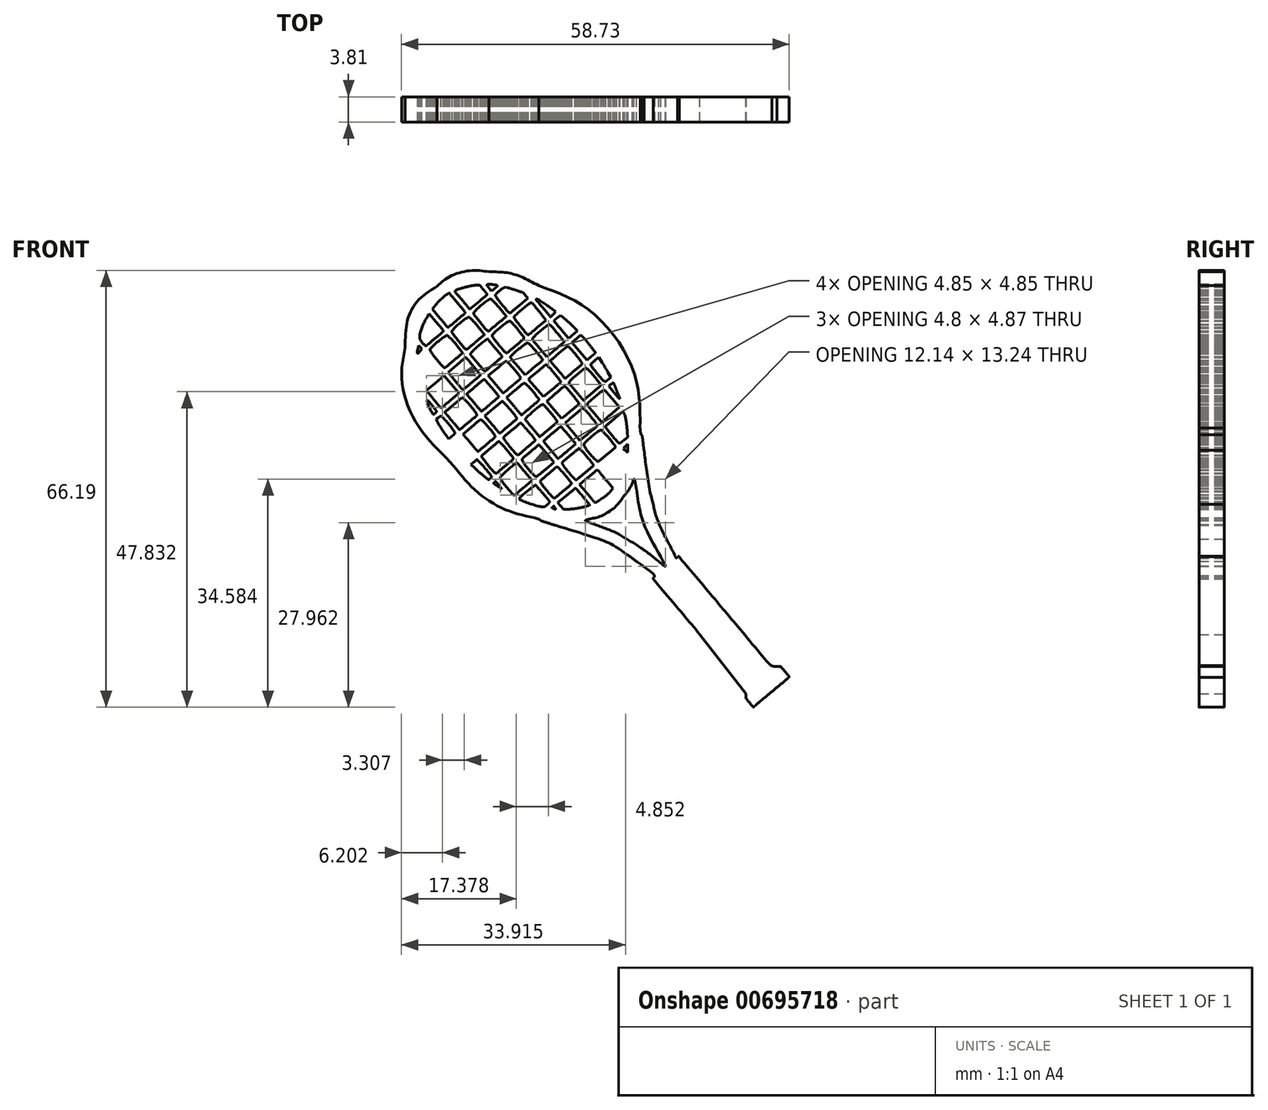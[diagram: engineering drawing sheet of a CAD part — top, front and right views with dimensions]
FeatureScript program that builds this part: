
annotation { "Feature Type Name" : "Feature", "Feature Type Description" : "" }
export const myFeature = defineFeature(function(context is Context, id is Id, definition is map)
    precondition{}
    {
        {
            var Q0;
            Q0=qCreatedBy(makeId("Front.planeOp"),FACE);
            var sketch = newSketch(context, id + "F0", { "sketchPlane" : qUnion([Q0])});
            skFitSpline(sketch, "E0", {"points": [v(8.3, -34.6) * mm, v(7.75, -33.92) * mm, v(7.73, -33.88) * mm, v(7.73, -33.21) * mm]});
            skFitSpline(sketch, "E1", {"points": [v(0.8, -24.26) * mm, v(-3.02, -19.72) * mm, v(-6.18, -15.94) * mm, v(-6.23, -15.86) * mm]});
            skFitSpline(sketch, "E2", {"points": [v(-6.23, -15.86) * mm, v(-6.27, -15.78) * mm, v(-6.25, -15.65) * mm, v(-6.18, -15.57) * mm]});
            skFitSpline(sketch, "E3", {"points": [v(-6.18, -15.57) * mm, v(-6.11, -15.48) * mm, v(-6.09, -15.36) * mm, v(-6.12, -15.3) * mm]});
            skFitSpline(sketch, "E4", {"points": [v(-6.12, -15.3) * mm, v(-6.22, -15.14) * mm, v(-8.37, -13.48) * mm, v(-9.44, -12.74) * mm]});
            skFitSpline(sketch, "E5", {"points": [v(-9.44, -12.74) * mm, v(-12.31, -10.75) * mm, v(-14.7, -9.72) * mm, v(-21.08, -7.72) * mm]});
            skFitSpline(sketch, "E6", {"points": [v(-21.08, -7.72) * mm, v(-22.32, -7.33) * mm, v(-23.37, -6.97) * mm, v(-23.4, -6.91) * mm]});
            skFitSpline(sketch, "E7", {"points": [v(-23.4, -6.91) * mm, v(-23.44, -6.86) * mm, v(-23.84, -6.7) * mm, v(-24.3, -6.57) * mm]});
            skFitSpline(sketch, "E8", {"points": [v(-24.3, -6.57) * mm, v(-28.9, -5.24) * mm, v(-33.33, -2.3) * mm, v(-37.04, 1.88) * mm]});
            skFitSpline(sketch, "E9", {"points": [v(-37.04, 1.88) * mm, v(-41.78, 7.22) * mm, v(-44.33, 13.72) * mm, v(-43.87, 19.25) * mm]});
            skFitSpline(sketch, "E10", {"points": [v(-43.87, 19.25) * mm, v(-43.53, 23.3) * mm, v(-41.98, 26.27) * mm, v(-39.04, 28.52) * mm]});
            skFitSpline(sketch, "E11", {"points": [v(-39.04, 28.52) * mm, v(-37.1, 30) * mm, v(-33.96, 30.88) * mm, v(-31.18, 30.72) * mm]});
            skFitSpline(sketch, "E12", {"points": [v(-31.18, 30.72) * mm, v(-28.5, 30.57) * mm, v(-26.4, 29.98) * mm, v(-23.61, 28.6) * mm]});
            skFitSpline(sketch, "E13", {"points": [v(-23.61, 28.6) * mm, v(-15.7, 24.66) * mm, v(-9.26, 15.6) * mm, v(-8.28, 7.03) * mm]});
            skFitSpline(sketch, "E14", {"points": [v(-8.28, 7.03) * mm, v(-8.22, 6.51) * mm, v(-8.13, 6.07) * mm, v(-8.08, 6.03) * mm]});
            skFitSpline(sketch, "E15", {"points": [v(-8.08, 6.03) * mm, v(-8.02, 6) * mm, v(-7.85, 4.93) * mm, v(-7.68, 3.65) * mm]});
            skFitSpline(sketch, "E16", {"points": [v(-7.68, 3.65) * mm, v(-7.3, 0.68) * mm, v(-6.69, -2.97) * mm, v(-6.3, -4.53) * mm]});
            skFitSpline(sketch, "E17", {"points": [v(-6.3, -4.53) * mm, v(-5.88, -6.16) * mm, v(-5.03, -8.3) * mm, v(-3.9, -10.52) * mm]});
            skFitSpline(sketch, "E18", {"points": [v(-3.9, -10.52) * mm, v(-2.82, -12.66) * mm, v(-2.8, -12.7) * mm, v(-2.57, -12.5) * mm]});
            skFitSpline(sketch, "E19", {"points": [v(-2.57, -12.5) * mm, v(-2.47, -12.42) * mm, v(-2.39, -12.42) * mm, v(-2.34, -12.49) * mm]});
            skFitSpline(sketch, "E20", {"points": [v(-2.34, -12.49) * mm, v(-2.3, -12.55) * mm, v(0.81, -16.27) * mm, v(4.58, -20.75) * mm]});
            skFitSpline(sketch, "E21", {"points": [v(4.58, -20.75) * mm, v(8.42, -25.33) * mm, v(11.53, -28.94) * mm, v(11.68, -29) * mm]});
            skFitSpline(sketch, "E22", {"points": [v(11.68, -29) * mm, v(11.82, -29.05) * mm, v(12.19, -29.1) * mm, v(12.48, -29.1) * mm]});
            skFitSpline(sketch, "E23", {"points": [v(12.48, -29.1) * mm, v(13.02, -29.1) * mm, v(13.03, -29.1) * mm, v(13.7, -29.89) * mm]});
            skFitSpline(sketch, "E24", {"points": [v(13.7, -29.89) * mm, v(14.06, -30.33) * mm, v(14.32, -30.72) * mm, v(14.28, -30.76) * mm]});
            skFitSpline(sketch, "E25", {"points": [v(14.28, -30.76) * mm, v(14.23, -30.8) * mm, v(13.1, -31.74) * mm, v(11.76, -32.85) * mm]});
            skFitSpline(sketch, "E26", {"points": [v(11.76, -32.85) * mm, v(10.43, -33.96) * mm, v(9.23, -34.97) * mm, v(9.1, -35.08) * mm]});
            skFitSpline(sketch, "E27", {"points": [v(9.1, -35.08) * mm, v(8.87, -35.29) * mm, v(8.86, -35.28) * mm, v(8.3, -34.6) * mm]});
            skLineSegment(sketch, "E28", {"start": v(7.73, -33.21) * mm, "end": v(7.73, -32.53) * mm});
            skLineSegment(sketch, "E29", {"start": v(0.8, -24.26) * mm, "end": v(7.73, -33.21) * mm});
            skFitSpline(sketch, "E30", {"points": [v(-5.17, -12.46) * mm, v(-7.27, -8.56) * mm, v(-8.18, -6.01) * mm, v(-8.85, -2.18) * mm]});
            skFitSpline(sketch, "E31", {"points": [v(-8.85, -2.18) * mm, v(-9, -1.37) * mm, v(-9.14, -0.71) * mm, v(-9.18, -0.71) * mm]});
            skFitSpline(sketch, "E32", {"points": [v(-9.18, -0.71) * mm, v(-9.22, -0.71) * mm, v(-9.3, -0.87) * mm, v(-9.38, -1.07) * mm]});
            skFitSpline(sketch, "E33", {"points": [v(-9.38, -1.07) * mm, v(-9.55, -1.57) * mm, v(-10.2, -2.63) * mm, v(-10.85, -3.45) * mm]});
            skFitSpline(sketch, "E34", {"points": [v(-10.85, -3.45) * mm, v(-11.95, -4.84) * mm, v(-14.11, -6.26) * mm, v(-15.87, -6.74) * mm]});
            skFitSpline(sketch, "E35", {"points": [v(-15.87, -6.74) * mm, v(-16.25, -6.85) * mm, v(-16.56, -6.96) * mm, v(-16.56, -7) * mm]});
            skFitSpline(sketch, "E36", {"points": [v(-16.56, -7) * mm, v(-16.56, -7.04) * mm, v(-15.9, -7.31) * mm, v(-15.1, -7.6) * mm]});
            skFitSpline(sketch, "E37", {"points": [v(-15.1, -7.6) * mm, v(-12.95, -8.4) * mm, v(-11.63, -9) * mm, v(-10.26, -9.82) * mm]});
            skFitSpline(sketch, "E38", {"points": [v(-10.26, -9.82) * mm, v(-8.87, -10.66) * mm, v(-6.9, -12.03) * mm, v(-5.48, -13.18) * mm]});
            skFitSpline(sketch, "E39", {"points": [v(-5.48, -13.18) * mm, v(-4.94, -13.61) * mm, v(-4.47, -13.95) * mm, v(-4.45, -13.92) * mm]});
            skFitSpline(sketch, "E40", {"points": [v(-4.45, -13.92) * mm, v(-4.42, -13.9) * mm, v(-4.75, -13.24) * mm, v(-5.17, -12.46) * mm]});
            skFitSpline(sketch, "E41", {"points": [v(-17.72, -5.12) * mm, v(-17.36, -5.06) * mm, v(-16.8, -4.93) * mm, v(-16.48, -4.84) * mm]});
            skFitSpline(sketch, "E42", {"points": [v(-16.48, -4.84) * mm, v(-15.96, -4.69) * mm, v(-15.9, -4.65) * mm, v(-16.03, -4.49) * mm]});
            skFitSpline(sketch, "E43", {"points": [v(-16.03, -4.49) * mm, v(-16.41, -4) * mm, v(-18.04, -2.1) * mm, v(-18.07, -2.1) * mm]});
            skFitSpline(sketch, "E44", {"points": [v(-18.07, -2.1) * mm, v(-18.1, -2.1) * mm, v(-18.7, -2.59) * mm, v(-19.42, -3.2) * mm]});
            skFitSpline(sketch, "E45", {"points": [v(-19.14, -5.27) * mm, v(-18.73, -5.25) * mm, v(-18.09, -5.18) * mm, v(-17.72, -5.12) * mm]});
            skLineSegment(sketch, "E46", {"start": v(-19.42, -3.2) * mm, "end": v(-20.74, -4.3) * mm});
            skLineSegment(sketch, "E47", {"start": v(-20.74, -4.3) * mm, "end": v(-20.32, -4.8) * mm});
            skLineSegment(sketch, "E48", {"start": v(-20.32, -4.8) * mm, "end": v(-19.9, -5.3) * mm});
            skLineSegment(sketch, "E49", {"start": v(-19.9, -5.3) * mm, "end": v(-19.14, -5.27) * mm});
            skFitSpline(sketch, "E50", {"points": [v(-21.2, -5.01) * mm, v(-21.3, -4.82) * mm, v(-21.36, -4.8) * mm, v(-21.5, -4.92) * mm]});
            skFitSpline(sketch, "E51", {"points": [v(-21.5, -4.92) * mm, v(-21.65, -5.05) * mm, v(-21.64, -5.07) * mm, v(-21.46, -5.14) * mm]});
            skFitSpline(sketch, "E52", {"points": [v(-21.46, -5.14) * mm, v(-21.13, -5.28) * mm, v(-21.08, -5.25) * mm, v(-21.2, -5.01) * mm]});
            skFitSpline(sketch, "E53", {"points": [v(-22.33, -4.57) * mm, v(-22.12, -4.38) * mm, v(-21.98, -4.17) * mm, v(-22.01, -4.1) * mm]});
            skFitSpline(sketch, "E54", {"points": [v(-22.01, -4.1) * mm, v(-22.04, -4.03) * mm, v(-22.52, -3.43) * mm, v(-23.08, -2.78) * mm]});
            skFitSpline(sketch, "E55", {"points": [v(-23.08, -2.78) * mm, v(-24, -1.7) * mm, v(-24.12, -1.6) * mm, v(-24.3, -1.73) * mm]});
            skFitSpline(sketch, "E56", {"points": [v(-24.3, -1.73) * mm, v(-24.73, -2.04) * mm, v(-26.5, -3.53) * mm, v(-26.5, -3.6) * mm]});
            skFitSpline(sketch, "E57", {"points": [v(-26.5, -3.6) * mm, v(-26.51, -3.74) * mm, v(-23.33, -4.88) * mm, v(-22.86, -4.9) * mm]});
            skFitSpline(sketch, "E58", {"points": [v(-22.86, -4.9) * mm, v(-22.77, -4.9) * mm, v(-22.53, -4.75) * mm, v(-22.33, -4.57) * mm]});
            skFitSpline(sketch, "E59", {"points": [v(-14.12, -3.7) * mm, v(-13.67, -3.4) * mm, v(-13.08, -2.93) * mm, v(-12.82, -2.65) * mm]});
            skFitSpline(sketch, "E60", {"points": [v(-12.88, -1.5) * mm, v(-14.17, 0.02) * mm, v(-14.69, 0.62) * mm, v(-14.75, 0.64) * mm]});
            skFitSpline(sketch, "E61", {"points": [v(-14.75, 0.64) * mm, v(-14.78, 0.66) * mm, v(-15.4, 0.18) * mm, v(-16.13, -0.42) * mm]});
            skLineSegment(sketch, "E62", {"start": v(-12.82, -2.65) * mm, "end": v(-12.35, -2.14) * mm});
            skLineSegment(sketch, "E63", {"start": v(-12.35, -2.14) * mm, "end": v(-12.88, -1.5) * mm});
            skFitSpline(sketch, "E64", {"points": [v(-16.92, -2.14) * mm, v(-16.63, -2.48) * mm, v(-16.13, -3.1) * mm, v(-15.8, -3.5) * mm]});
            skFitSpline(sketch, "E65", {"points": [v(-15.8, -3.5) * mm, v(-15.46, -3.9) * mm, v(-15.13, -4.23) * mm, v(-15.07, -4.24) * mm]});
            skFitSpline(sketch, "E66", {"points": [v(-15.07, -4.24) * mm, v(-15, -4.24) * mm, v(-14.58, -4) * mm, v(-14.12, -3.7) * mm]});
            skLineSegment(sketch, "E67", {"start": v(-16.13, -0.42) * mm, "end": v(-17.44, -1.51) * mm});
            skLineSegment(sketch, "E68", {"start": v(-17.44, -1.51) * mm, "end": v(-16.92, -2.14) * mm});
            skFitSpline(sketch, "E69", {"points": [v(-19.91, -2.53) * mm, v(-19.22, -1.94) * mm, v(-18.67, -1.42) * mm, v(-18.68, -1.37) * mm]});
            skFitSpline(sketch, "E70", {"points": [v(-18.68, -1.37) * mm, v(-18.73, -1.25) * mm, v(-20.53, 0.9) * mm, v(-20.72, 1.06) * mm]});
            skFitSpline(sketch, "E71", {"points": [v(-20.72, 1.06) * mm, v(-20.83, 1.15) * mm, v(-21.17, 0.92) * mm, v(-22.14, 0.1) * mm]});
            skFitSpline(sketch, "E72", {"points": [v(-22.14, 0.1) * mm, v(-22.84, -0.5) * mm, v(-23.4, -1.03) * mm, v(-23.38, -1.08) * mm]});
            skFitSpline(sketch, "E73", {"points": [v(-23.38, -1.08) * mm, v(-23.32, -1.27) * mm, v(-21.37, -3.57) * mm, v(-21.27, -3.58) * mm]});
            skFitSpline(sketch, "E74", {"points": [v(-21.27, -3.58) * mm, v(-21.22, -3.58) * mm, v(-20.6, -3.1) * mm, v(-19.91, -2.53) * mm]});
            skFitSpline(sketch, "E75", {"points": [v(-25.75, 0.4) * mm, v(-26.36, 1.12) * mm, v(-26.88, 1.72) * mm, v(-26.89, 1.72) * mm]});
            skFitSpline(sketch, "E76", {"points": [v(-26.89, 1.72) * mm, v(-27.02, 1.72) * mm, v(-29.43, -0.43) * mm, v(-29.42, -0.54) * mm]});
            skFitSpline(sketch, "E77", {"points": [v(-29.42, -0.54) * mm, v(-29.4, -0.67) * mm, v(-27.39, -3.14) * mm, v(-27.3, -3.14) * mm]});
            skFitSpline(sketch, "E78", {"points": [v(-27.3, -3.14) * mm, v(-27.28, -3.14) * mm, v(-26.67, -2.64) * mm, v(-25.95, -2.03) * mm]});
            skLineSegment(sketch, "E79", {"start": v(-25.95, -2.03) * mm, "end": v(-24.63, -0.91) * mm});
            skLineSegment(sketch, "E80", {"start": v(-24.63, -0.91) * mm, "end": v(-25.75, 0.4) * mm});
            skFitSpline(sketch, "E81", {"points": [v(-29.7, -1.6) * mm, v(-29.96, -1.3) * mm, v(-30.18, -1.04) * mm, v(-30.2, -1.04) * mm]});
            skFitSpline(sketch, "E82", {"points": [v(-30.2, -1.04) * mm, v(-30.22, -1.04) * mm, v(-30.3, -1.11) * mm, v(-30.36, -1.2) * mm]});
            skFitSpline(sketch, "E83", {"points": [v(-30.36, -1.2) * mm, v(-30.47, -1.33) * mm, v(-30.39, -1.43) * mm, v(-29.9, -1.75) * mm]});
            skFitSpline(sketch, "E84", {"points": [v(-29.9, -1.75) * mm, v(-29.59, -1.97) * mm, v(-29.3, -2.15) * mm, v(-29.28, -2.15) * mm]});
            skFitSpline(sketch, "E85", {"points": [v(-29.28, -2.15) * mm, v(-29.26, -2.15) * mm, v(-29.45, -1.9) * mm, v(-29.7, -1.6) * mm]});
            skFitSpline(sketch, "E86", {"points": [v(-11.26, -0.36) * mm, v(-11.08, -0.01) * mm, v(-10.8, 0.7) * mm, v(-10.66, 1.22) * mm]});
            skFitSpline(sketch, "E87", {"points": [v(-10.66, 1.22) * mm, v(-10.35, 2.28) * mm, v(-10.33, 2.19) * mm, v(-11.06, 3.03) * mm]});
            skFitSpline(sketch, "E88", {"points": [v(-12.8, 2.37) * mm, v(-14.15, 1.25) * mm, v(-14.15, 1.25) * mm, v(-13.94, 1.01) * mm]});
            skFitSpline(sketch, "E89", {"points": [v(-13.94, 1.01) * mm, v(-13.82, 0.88) * mm, v(-13.31, 0.29) * mm, v(-12.8, -0.31) * mm]});
            skFitSpline(sketch, "E90", {"points": [v(-12.8, -0.31) * mm, v(-11.76, -1.54) * mm, v(-11.86, -1.54) * mm, v(-11.26, -0.36) * mm]});
            skLineSegment(sketch, "E91", {"start": v(-11.06, 3.03) * mm, "end": v(-11.46, 3.5) * mm});
            skLineSegment(sketch, "E92", {"start": v(-11.46, 3.5) * mm, "end": v(-12.8, 2.37) * mm});
            skFitSpline(sketch, "E93", {"points": [v(-30.81, -0.36) * mm, v(-30.81, -0.28) * mm, v(-32.37, 1.63) * mm, v(-32.84, 2.13) * mm]});
            skFitSpline(sketch, "E94", {"points": [v(-32.84, 2.13) * mm, v(-32.95, 2.24) * mm, v(-33.07, 2.2) * mm, v(-33.43, 1.88) * mm]});
            skFitSpline(sketch, "E95", {"points": [v(-33.26, 0.9) * mm, v(-32.91, 0.59) * mm, v(-32.32, 0.06) * mm, v(-31.93, -0.25) * mm]});
            skFitSpline(sketch, "E96", {"points": [v(-31.93, -0.25) * mm, v(-31.26, -0.8) * mm, v(-31.21, -0.82) * mm, v(-31.02, -0.64) * mm]});
            skFitSpline(sketch, "E97", {"points": [v(-31.02, -0.64) * mm, v(-30.9, -0.54) * mm, v(-30.81, -0.41) * mm, v(-30.81, -0.36) * mm]});
            skLineSegment(sketch, "E98", {"start": v(-33.43, 1.88) * mm, "end": v(-33.88, 1.5) * mm});
            skLineSegment(sketch, "E99", {"start": v(-33.88, 1.5) * mm, "end": v(-33.26, 0.9) * mm});
            skFitSpline(sketch, "E100", {"points": [v(-16.61, 0.24) * mm, v(-15.91, 0.83) * mm, v(-15.36, 1.35) * mm, v(-15.37, 1.4) * mm]});
            skFitSpline(sketch, "E101", {"points": [v(-15.37, 1.4) * mm, v(-15.42, 1.53) * mm, v(-17.07, 3.52) * mm, v(-17.33, 3.75) * mm]});
            skFitSpline(sketch, "E102", {"points": [v(-17.33, 3.75) * mm, v(-17.55, 3.95) * mm, v(-17.58, 3.93) * mm, v(-18.83, 2.88) * mm]});
            skFitSpline(sketch, "E103", {"points": [v(-18.83, 2.88) * mm, v(-19.53, 2.28) * mm, v(-20.1, 1.75) * mm, v(-20.07, 1.69) * mm]});
            skFitSpline(sketch, "E104", {"points": [v(-20.07, 1.69) * mm, v(-20, 1.5) * mm, v(-18.06, -0.8) * mm, v(-17.97, -0.82) * mm]});
            skFitSpline(sketch, "E105", {"points": [v(-17.97, -0.82) * mm, v(-17.92, -0.82) * mm, v(-17.3, -0.34) * mm, v(-16.61, 0.24) * mm]});
            skFitSpline(sketch, "E106", {"points": [v(-22.44, 3.17) * mm, v(-23.05, 3.89) * mm, v(-23.57, 4.48) * mm, v(-23.6, 4.48) * mm]});
            skFitSpline(sketch, "E107", {"points": [v(-23.6, 4.48) * mm, v(-23.62, 4.48) * mm, v(-24.21, 4) * mm, v(-24.9, 3.4) * mm]});
            skFitSpline(sketch, "E108", {"points": [v(-24.9, 3.4) * mm, v(-25.66, 2.77) * mm, v(-26.16, 2.27) * mm, v(-26.12, 2.19) * mm]});
            skFitSpline(sketch, "E109", {"points": [v(-26.12, 2.19) * mm, v(-26, 1.87) * mm, v(-24.02, -0.36) * mm, v(-23.91, -0.3) * mm]});
            skFitSpline(sketch, "E110", {"points": [v(-23.91, -0.3) * mm, v(-23.85, -0.26) * mm, v(-23.24, 0.24) * mm, v(-22.56, 0.81) * mm]});
            skLineSegment(sketch, "E111", {"start": v(-22.56, 0.81) * mm, "end": v(-21.32, 1.85) * mm});
            skLineSegment(sketch, "E112", {"start": v(-21.32, 1.85) * mm, "end": v(-22.44, 3.17) * mm});
            skFitSpline(sketch, "E113", {"points": [v(-28.76, 1.24) * mm, v(-28.07, 1.82) * mm, v(-27.5, 2.35) * mm, v(-27.5, 2.4) * mm]});
            skFitSpline(sketch, "E114", {"points": [v(-27.5, 2.4) * mm, v(-27.5, 2.48) * mm, v(-29.06, 4.4) * mm, v(-29.54, 4.9) * mm]});
            skFitSpline(sketch, "E115", {"points": [v(-29.54, 4.9) * mm, v(-29.65, 5.02) * mm, v(-29.9, 4.85) * mm, v(-30.93, 3.98) * mm]});
            skFitSpline(sketch, "E116", {"points": [v(-30.93, 3.98) * mm, v(-31.62, 3.4) * mm, v(-32.2, 2.87) * mm, v(-32.23, 2.82) * mm]});
            skFitSpline(sketch, "E117", {"points": [v(-32.23, 2.82) * mm, v(-32.26, 2.73) * mm, v(-30.17, 0.17) * mm, v(-30.07, 0.17) * mm]});
            skFitSpline(sketch, "E118", {"points": [v(-30.07, 0.17) * mm, v(-30.04, 0.17) * mm, v(-29.45, 0.65) * mm, v(-28.76, 1.24) * mm]});
            skFitSpline(sketch, "E119", {"points": [v(-13.25, 3.06) * mm, v(-12.58, 3.61) * mm, v(-12.04, 4.1) * mm, v(-12.04, 4.14) * mm]});
            skFitSpline(sketch, "E120", {"points": [v(-12.04, 4.14) * mm, v(-12.04, 4.24) * mm, v(-14.14, 6.69) * mm, v(-14.22, 6.69) * mm]});
            skFitSpline(sketch, "E121", {"points": [v(-14.22, 6.69) * mm, v(-14.38, 6.69) * mm, v(-16.8, 4.56) * mm, v(-16.76, 4.46) * mm]});
            skFitSpline(sketch, "E122", {"points": [v(-16.76, 4.46) * mm, v(-16.67, 4.17) * mm, v(-14.73, 1.96) * mm, v(-14.6, 2) * mm]});
            skFitSpline(sketch, "E123", {"points": [v(-14.6, 2) * mm, v(-14.53, 2.02) * mm, v(-13.92, 2.5) * mm, v(-13.25, 3.06) * mm]});
            skFitSpline(sketch, "E124", {"points": [v(-33.64, 2.97) * mm, v(-33.65, 3.06) * mm, v(-34.12, 3.68) * mm, v(-34.68, 4.35) * mm]});
            skFitSpline(sketch, "E125", {"points": [v(-34.68, 4.35) * mm, v(-35.81, 5.68) * mm, v(-35.69, 5.63) * mm, v(-36.43, 5) * mm]});
            skFitSpline(sketch, "E126", {"points": [v(-36.22, 4) * mm, v(-35.9, 3.63) * mm, v(-35.39, 3.04) * mm, v(-35.08, 2.7) * mm]});
            skLineSegment(sketch, "E127", {"start": v(-36.43, 5) * mm, "end": v(-36.8, 4.7) * mm});
            skLineSegment(sketch, "E128", {"start": v(-36.8, 4.7) * mm, "end": v(-36.22, 4) * mm});
            skFitSpline(sketch, "E129", {"points": [v(-34.07, 2.44) * mm, v(-33.83, 2.64) * mm, v(-33.63, 2.88) * mm, v(-33.64, 2.97) * mm]});
            skLineSegment(sketch, "E130", {"start": v(-35.08, 2.7) * mm, "end": v(-34.5, 2.08) * mm});
            skLineSegment(sketch, "E131", {"start": v(-34.5, 2.08) * mm, "end": v(-34.07, 2.44) * mm});
            skFitSpline(sketch, "E132", {"points": [v(-19.12, 5.93) * mm, v(-19.73, 6.65) * mm, v(-20.26, 7.24) * mm, v(-20.29, 7.24) * mm]});
            skFitSpline(sketch, "E133", {"points": [v(-20.29, 7.24) * mm, v(-20.32, 7.24) * mm, v(-20.91, 6.76) * mm, v(-21.6, 6.17) * mm]});
            skFitSpline(sketch, "E134", {"points": [v(-21.6, 6.17) * mm, v(-22.41, 5.5) * mm, v(-22.85, 5.05) * mm, v(-22.81, 4.95) * mm]});
            skFitSpline(sketch, "E135", {"points": [v(-22.81, 4.95) * mm, v(-22.78, 4.87) * mm, v(-22.3, 4.26) * mm, v(-21.74, 3.6) * mm]});
            skFitSpline(sketch, "E136", {"points": [v(-21.74, 3.6) * mm, v(-20.86, 2.56) * mm, v(-20.7, 2.41) * mm, v(-20.54, 2.52) * mm]});
            skFitSpline(sketch, "E137", {"points": [v(-20.54, 2.52) * mm, v(-20.44, 2.6) * mm, v(-19.83, 3.1) * mm, v(-19.18, 3.64) * mm]});
            skLineSegment(sketch, "E138", {"start": v(-19.18, 3.64) * mm, "end": v(-18.01, 4.62) * mm});
            skLineSegment(sketch, "E139", {"start": v(-18.01, 4.62) * mm, "end": v(-19.12, 5.93) * mm});
            skFitSpline(sketch, "E140", {"points": [v(-25.5, 3.99) * mm, v(-24.8, 4.57) * mm, v(-24.22, 5.09) * mm, v(-24.2, 5.15) * mm]});
            skFitSpline(sketch, "E141", {"points": [v(-24.2, 5.15) * mm, v(-24.17, 5.23) * mm, v(-25.42, 6.78) * mm, v(-26.18, 7.61) * mm]});
            skFitSpline(sketch, "E142", {"points": [v(-26.18, 7.61) * mm, v(-26.37, 7.81) * mm, v(-26.41, 7.79) * mm, v(-27.65, 6.74) * mm]});
            skFitSpline(sketch, "E143", {"points": [v(-27.65, 6.74) * mm, v(-28.36, 6.14) * mm, v(-28.93, 5.61) * mm, v(-28.93, 5.56) * mm]});
            skFitSpline(sketch, "E144", {"points": [v(-28.93, 5.56) * mm, v(-28.93, 5.47) * mm, v(-26.84, 2.93) * mm, v(-26.77, 2.93) * mm]});
            skFitSpline(sketch, "E145", {"points": [v(-26.77, 2.93) * mm, v(-26.75, 2.93) * mm, v(-26.18, 3.4) * mm, v(-25.5, 3.99) * mm]});
            skFitSpline(sketch, "E146", {"points": [v(-10.57, 3.7) * mm, v(-10.43, 3.52) * mm, v(-10.29, 3.38) * mm, v(-10.24, 3.38) * mm]});
            skFitSpline(sketch, "E147", {"points": [v(-10.24, 3.38) * mm, v(-10.2, 3.38) * mm, v(-10.16, 3.66) * mm, v(-10.16, 4) * mm]});
            skLineSegment(sketch, "E148", {"start": v(-10.16, 4) * mm, "end": v(-10.16, 4.63) * mm});
            skLineSegment(sketch, "E149", {"start": v(-10.16, 4.63) * mm, "end": v(-10.49, 4.32) * mm});
            skLineSegment(sketch, "E150", {"start": v(-10.49, 4.32) * mm, "end": v(-10.81, 4) * mm});
            skLineSegment(sketch, "E151", {"start": v(-10.81, 4) * mm, "end": v(-10.57, 3.7) * mm});
            skFitSpline(sketch, "E152", {"points": [v(-31.52, 4.55) * mm, v(-30.83, 5.14) * mm, v(-30.26, 5.66) * mm, v(-30.26, 5.7) * mm]});
            skFitSpline(sketch, "E153", {"points": [v(-30.26, 5.7) * mm, v(-30.26, 5.85) * mm, v(-32.38, 8.29) * mm, v(-32.48, 8.26) * mm]});
            skFitSpline(sketch, "E154", {"points": [v(-32.48, 8.26) * mm, v(-32.54, 8.24) * mm, v(-33.16, 7.75) * mm, v(-33.85, 7.17) * mm]});
            skFitSpline(sketch, "E155", {"points": [v(-34, 4.8) * mm, v(-33.38, 4.07) * mm, v(-32.86, 3.48) * mm, v(-32.84, 3.48) * mm]});
            skFitSpline(sketch, "E156", {"points": [v(-32.84, 3.48) * mm, v(-32.8, 3.48) * mm, v(-32.22, 3.97) * mm, v(-31.52, 4.55) * mm]});
            skLineSegment(sketch, "E157", {"start": v(-33.85, 7.17) * mm, "end": v(-35.1, 6.1) * mm});
            skLineSegment(sketch, "E158", {"start": v(-35.1, 6.1) * mm, "end": v(-34, 4.8) * mm});
            skFitSpline(sketch, "E159", {"points": [v(-10.2, 6.41) * mm, v(-10.3, 7.4) * mm, v(-10.6, 9) * mm, v(-10.76, 9.3) * mm]});
            skFitSpline(sketch, "E160", {"points": [v(-10.76, 9.3) * mm, v(-10.87, 9.54) * mm, v(-10.93, 9.51) * mm, v(-12.2, 8.43) * mm]});
            skFitSpline(sketch, "E161", {"points": [v(-12.2, 8.43) * mm, v(-12.93, 7.82) * mm, v(-13.51, 7.29) * mm, v(-13.5, 7.25) * mm]});
            skFitSpline(sketch, "E162", {"points": [v(-13.5, 7.25) * mm, v(-13.42, 7.06) * mm, v(-11.42, 4.72) * mm, v(-11.35, 4.73) * mm]});
            skFitSpline(sketch, "E163", {"points": [v(-11.35, 4.73) * mm, v(-11.3, 4.74) * mm, v(-11.01, 4.95) * mm, v(-10.7, 5.2) * mm]});
            skLineSegment(sketch, "E164", {"start": v(-10.7, 5.2) * mm, "end": v(-10.14, 5.64) * mm});
            skLineSegment(sketch, "E165", {"start": v(-10.14, 5.64) * mm, "end": v(-10.2, 6.41) * mm});
            skFitSpline(sketch, "E166", {"points": [v(-15.85, 6.43) * mm, v(-15.28, 6.9) * mm, v(-14.8, 7.34) * mm, v(-14.8, 7.4) * mm]});
            skFitSpline(sketch, "E167", {"points": [v(-14.8, 7.4) * mm, v(-14.8, 7.5) * mm, v(-16.88, 10) * mm, v(-16.99, 10) * mm]});
            skFitSpline(sketch, "E168", {"points": [v(-16.99, 10) * mm, v(-17.03, 10) * mm, v(-17.64, 9.5) * mm, v(-18.35, 8.9) * mm]});
            skFitSpline(sketch, "E169", {"points": [v(-17.15, 5.36) * mm, v(-17, 5.47) * mm, v(-16.42, 5.95) * mm, v(-15.85, 6.43) * mm]});
            skLineSegment(sketch, "E170", {"start": v(-18.35, 8.9) * mm, "end": v(-19.64, 7.82) * mm});
            skLineSegment(sketch, "E171", {"start": v(-19.64, 7.82) * mm, "end": v(-18.52, 6.49) * mm});
            skLineSegment(sketch, "E172", {"start": v(-18.52, 6.49) * mm, "end": v(-17.4, 5.16) * mm});
            skLineSegment(sketch, "E173", {"start": v(-17.4, 5.16) * mm, "end": v(-17.15, 5.36) * mm});
            skFitSpline(sketch, "E174", {"points": [v(-36.37, 6.2) * mm, v(-36.33, 6.3) * mm, v(-38.36, 8.78) * mm, v(-38.5, 8.8) * mm]});
            skFitSpline(sketch, "E175", {"points": [v(-38.5, 8.8) * mm, v(-38.53, 8.8) * mm, v(-38.7, 8.7) * mm, v(-38.88, 8.58) * mm]});
            skFitSpline(sketch, "E176", {"points": [v(-38.7, 7.5) * mm, v(-38.42, 7.03) * mm, v(-37.99, 6.36) * mm, v(-37.74, 6) * mm]});
            skLineSegment(sketch, "E177", {"start": v(-38.88, 8.58) * mm, "end": v(-39.2, 8.34) * mm});
            skLineSegment(sketch, "E178", {"start": v(-39.2, 8.34) * mm, "end": v(-38.7, 7.5) * mm});
            skFitSpline(sketch, "E179", {"points": [v(-36.84, 5.73) * mm, v(-36.6, 5.93) * mm, v(-36.38, 6.14) * mm, v(-36.37, 6.2) * mm]});
            skLineSegment(sketch, "E180", {"start": v(-37.74, 6) * mm, "end": v(-37.29, 5.37) * mm});
            skLineSegment(sketch, "E181", {"start": v(-37.29, 5.37) * mm, "end": v(-36.84, 5.73) * mm});
            skFitSpline(sketch, "E182", {"points": [v(-22.03, 6.9) * mm, v(-21.42, 7.4) * mm, v(-20.91, 7.87) * mm, v(-20.9, 7.92) * mm]});
            skFitSpline(sketch, "E183", {"points": [v(-20.9, 7.92) * mm, v(-20.86, 8) * mm, v(-22.95, 10.55) * mm, v(-23.06, 10.55) * mm]});
            skFitSpline(sketch, "E184", {"points": [v(-23.06, 10.55) * mm, v(-23.17, 10.55) * mm, v(-25.62, 8.43) * mm, v(-25.62, 8.33) * mm]});
            skFitSpline(sketch, "E185", {"points": [v(-25.62, 8.33) * mm, v(-25.62, 8.27) * mm, v(-25.14, 7.65) * mm, v(-24.55, 6.96) * mm]});
            skFitSpline(sketch, "E186", {"points": [v(-24.55, 6.96) * mm, v(-23.64, 5.87) * mm, v(-23.46, 5.71) * mm, v(-23.31, 5.83) * mm]});
            skFitSpline(sketch, "E187", {"points": [v(-23.31, 5.83) * mm, v(-23.21, 5.9) * mm, v(-22.64, 6.38) * mm, v(-22.03, 6.9) * mm]});
            skFitSpline(sketch, "E188", {"points": [v(-28.25, 7.3) * mm, v(-27.56, 7.88) * mm, v(-26.99, 8.4) * mm, v(-26.97, 8.44) * mm]});
            skFitSpline(sketch, "E189", {"points": [v(-26.97, 8.44) * mm, v(-26.95, 8.5) * mm, v(-28.5, 10.44) * mm, v(-29.05, 11.04) * mm]});
            skFitSpline(sketch, "E190", {"points": [v(-29.05, 11.04) * mm, v(-29.1, 11.09) * mm, v(-29.74, 10.62) * mm, v(-30.47, 10) * mm]});
            skFitSpline(sketch, "E191", {"points": [v(-30.69, 7.56) * mm, v(-30.07, 6.84) * mm, v(-29.56, 6.24) * mm, v(-29.54, 6.24) * mm]});
            skFitSpline(sketch, "E192", {"points": [v(-29.54, 6.24) * mm, v(-29.52, 6.24) * mm, v(-28.94, 6.72) * mm, v(-28.25, 7.3) * mm]});
            skLineSegment(sketch, "E193", {"start": v(-30.47, 10) * mm, "end": v(-31.8, 8.87) * mm});
            skLineSegment(sketch, "E194", {"start": v(-31.8, 8.87) * mm, "end": v(-30.69, 7.56) * mm});
            skFitSpline(sketch, "E195", {"points": [v(-34.28, 7.87) * mm, v(-33.59, 8.46) * mm, v(-33.02, 8.96) * mm, v(-33.02, 9) * mm]});
            skFitSpline(sketch, "E196", {"points": [v(-33.02, 9) * mm, v(-33.03, 9.14) * mm, v(-35.16, 11.6) * mm, v(-35.25, 11.57) * mm]});
            skFitSpline(sketch, "E197", {"points": [v(-35.25, 11.57) * mm, v(-35.3, 11.55) * mm, v(-35.92, 11.06) * mm, v(-36.62, 10.47) * mm]});
            skFitSpline(sketch, "E198", {"points": [v(-36.62, 10.47) * mm, v(-37.86, 9.42) * mm, v(-37.88, 9.4) * mm, v(-37.68, 9.18) * mm]});
            skFitSpline(sketch, "E199", {"points": [v(-37.68, 9.18) * mm, v(-37.57, 9.05) * mm, v(-37.07, 8.47) * mm, v(-36.56, 7.87) * mm]});
            skFitSpline(sketch, "E200", {"points": [v(-36.56, 7.87) * mm, v(-36.06, 7.28) * mm, v(-35.63, 6.8) * mm, v(-35.6, 6.8) * mm]});
            skFitSpline(sketch, "E201", {"points": [v(-35.6, 6.8) * mm, v(-35.57, 6.8) * mm, v(-34.98, 7.28) * mm, v(-34.28, 7.87) * mm]});
            skFitSpline(sketch, "E202", {"points": [v(-12.52, 11.47) * mm, v(-13.11, 12.18) * mm, v(-13.64, 12.76) * mm, v(-13.68, 12.76) * mm]});
            skFitSpline(sketch, "E203", {"points": [v(-13.68, 12.76) * mm, v(-13.8, 12.76) * mm, v(-16.3, 10.65) * mm, v(-16.27, 10.57) * mm]});
            skFitSpline(sketch, "E204", {"points": [v(-16.27, 10.57) * mm, v(-16.26, 10.53) * mm, v(-15.76, 9.92) * mm, v(-15.17, 9.2) * mm]});
            skLineSegment(sketch, "E205", {"start": v(-11.98, 9.7) * mm, "end": v(-11.43, 10.19) * mm});
            skLineSegment(sketch, "E206", {"start": v(-11.43, 10.19) * mm, "end": v(-12.52, 11.47) * mm});
            skFitSpline(sketch, "E207", {"points": [v(-13.32, 8.57) * mm, v(-12.89, 8.92) * mm, v(-12.29, 9.43) * mm, v(-11.98, 9.7) * mm]});
            skLineSegment(sketch, "E208", {"start": v(-15.17, 9.2) * mm, "end": v(-14.1, 7.92) * mm});
            skLineSegment(sketch, "E209", {"start": v(-14.1, 7.92) * mm, "end": v(-13.32, 8.57) * mm});
            skFitSpline(sketch, "E210", {"points": [v(-18.5, 9.83) * mm, v(-18, 10.26) * mm, v(-17.57, 10.65) * mm, v(-17.56, 10.7) * mm]});
            skFitSpline(sketch, "E211", {"points": [v(-17.56, 10.7) * mm, v(-17.56, 10.8) * mm, v(-19.66, 13.31) * mm, v(-19.75, 13.31) * mm]});
            skFitSpline(sketch, "E212", {"points": [v(-19.75, 13.31) * mm, v(-19.8, 13.31) * mm, v(-20.43, 12.8) * mm, v(-21.61, 11.8) * mm]});
            skFitSpline(sketch, "E213", {"points": [v(-19.81, 8.76) * mm, v(-19.61, 8.93) * mm, v(-19.02, 9.4) * mm, v(-18.5, 9.83) * mm]});
            skLineSegment(sketch, "E214", {"start": v(-21.61, 11.8) * mm, "end": v(-22.42, 11.12) * mm});
            skLineSegment(sketch, "E215", {"start": v(-22.42, 11.12) * mm, "end": v(-21.3, 9.8) * mm});
            skLineSegment(sketch, "E216", {"start": v(-21.3, 9.8) * mm, "end": v(-20.18, 8.46) * mm});
            skLineSegment(sketch, "E217", {"start": v(-20.18, 8.46) * mm, "end": v(-19.81, 8.76) * mm});
            skFitSpline(sketch, "E218", {"points": [v(-24.8, 10.2) * mm, v(-24.19, 10.72) * mm, v(-23.67, 11.17) * mm, v(-23.65, 11.22) * mm]});
            skFitSpline(sketch, "E219", {"points": [v(-23.65, 11.22) * mm, v(-23.61, 11.32) * mm, v(-25.7, 13.8) * mm, v(-25.84, 13.8) * mm]});
            skFitSpline(sketch, "E220", {"points": [v(-25.84, 13.8) * mm, v(-25.9, 13.8) * mm, v(-26.51, 13.32) * mm, v(-27.22, 12.73) * mm]});
            skFitSpline(sketch, "E221", {"points": [v(-27.38, 10.32) * mm, v(-26.4, 9.18) * mm, v(-26.23, 9.02) * mm, v(-26.08, 9.14) * mm]});
            skFitSpline(sketch, "E222", {"points": [v(-26.08, 9.14) * mm, v(-25.98, 9.22) * mm, v(-25.4, 9.7) * mm, v(-24.8, 10.2) * mm]});
            skLineSegment(sketch, "E223", {"start": v(-27.22, 12.73) * mm, "end": v(-28.5, 11.64) * mm});
            skLineSegment(sketch, "E224", {"start": v(-28.5, 11.64) * mm, "end": v(-27.38, 10.32) * mm});
            skFitSpline(sketch, "E225", {"points": [v(-39.26, 9.33) * mm, v(-39.08, 9.54) * mm, v(-39.08, 9.56) * mm, v(-39.27, 9.8) * mm]});
            skFitSpline(sketch, "E226", {"points": [v(-39.27, 9.8) * mm, v(-39.84, 10.52) * mm, v(-40.46, 11.21) * mm, v(-40.5, 11.17) * mm]});
            skFitSpline(sketch, "E227", {"points": [v(-40.5, 11.17) * mm, v(-40.56, 11.11) * mm, v(-39.63, 9.12) * mm, v(-39.54, 9.12) * mm]});
            skFitSpline(sketch, "E228", {"points": [v(-39.54, 9.12) * mm, v(-39.5, 9.12) * mm, v(-39.37, 9.21) * mm, v(-39.26, 9.33) * mm]});
            skFitSpline(sketch, "E229", {"points": [v(-31.01, 10.61) * mm, v(-30.32, 11.2) * mm, v(-29.75, 11.7) * mm, v(-29.73, 11.75) * mm]});
            skFitSpline(sketch, "E230", {"points": [v(-29.73, 11.75) * mm, v(-29.71, 11.8) * mm, v(-31.2, 13.65) * mm, v(-31.87, 14.4) * mm]});
            skFitSpline(sketch, "E231", {"points": [v(-31.87, 14.4) * mm, v(-31.88, 14.42) * mm, v(-32.5, 13.93) * mm, v(-33.24, 13.3) * mm]});
            skFitSpline(sketch, "E232", {"points": [v(-33.24, 13.3) * mm, v(-34.56, 12.18) * mm, v(-34.57, 12.17) * mm, v(-34.37, 11.94) * mm]});
            skFitSpline(sketch, "E233", {"points": [v(-34.37, 11.94) * mm, v(-34.26, 11.82) * mm, v(-33.75, 11.23) * mm, v(-33.25, 10.63) * mm]});
            skFitSpline(sketch, "E234", {"points": [v(-33.25, 10.63) * mm, v(-32.75, 10.04) * mm, v(-32.32, 9.56) * mm, v(-32.3, 9.56) * mm]});
            skFitSpline(sketch, "E235", {"points": [v(-32.3, 9.56) * mm, v(-32.28, 9.56) * mm, v(-31.7, 10.03) * mm, v(-31.01, 10.61) * mm]});
            skLineSegment(sketch, "E236", {"start": v(-39.26, 9.33) * mm, "end": v(-39.26, 9.33) * mm});
            skFitSpline(sketch, "E237", {"points": [v(-37.04, 11.18) * mm, v(-36.35, 11.77) * mm, v(-35.78, 12.28) * mm, v(-35.78, 12.31) * mm]});
            skFitSpline(sketch, "E238", {"points": [v(-35.78, 12.31) * mm, v(-35.78, 12.35) * mm, v(-36.28, 12.96) * mm, v(-36.88, 13.67) * mm]});
            skFitSpline(sketch, "E239", {"points": [v(-40.39, 12.42) * mm, v(-39.56, 11.38) * mm, v(-38.47, 10.12) * mm, v(-38.4, 10.12) * mm]});
            skFitSpline(sketch, "E240", {"points": [v(-38.4, 10.12) * mm, v(-38.35, 10.11) * mm, v(-37.74, 10.6) * mm, v(-37.04, 11.18) * mm]});
            skLineSegment(sketch, "E241", {"start": v(-36.88, 13.67) * mm, "end": v(-37.97, 14.97) * mm});
            skLineSegment(sketch, "E242", {"start": v(-37.97, 14.97) * mm, "end": v(-39.3, 13.85) * mm});
            skLineSegment(sketch, "E243", {"start": v(-39.3, 13.85) * mm, "end": v(-40.63, 12.73) * mm});
            skLineSegment(sketch, "E244", {"start": v(-40.63, 12.73) * mm, "end": v(-40.39, 12.42) * mm});
            skFitSpline(sketch, "E245", {"points": [v(-15.32, 12.53) * mm, v(-14.73, 13.03) * mm, v(-14.25, 13.47) * mm, v(-14.25, 13.5) * mm]});
            skFitSpline(sketch, "E246", {"points": [v(-14.25, 13.5) * mm, v(-14.25, 13.58) * mm, v(-16.37, 16.07) * mm, v(-16.45, 16.07) * mm]});
            skFitSpline(sketch, "E247", {"points": [v(-16.45, 16.07) * mm, v(-16.59, 16.07) * mm, v(-19.05, 13.94) * mm, v(-19.02, 13.85) * mm]});
            skFitSpline(sketch, "E248", {"points": [v(-19.02, 13.85) * mm, v(-19, 13.8) * mm, v(-18.51, 13.19) * mm, v(-17.92, 12.49) * mm]});
            skFitSpline(sketch, "E249", {"points": [v(-17.92, 12.49) * mm, v(-16.87, 11.23) * mm, v(-16.85, 11.22) * mm, v(-16.63, 11.42) * mm]});
            skFitSpline(sketch, "E250", {"points": [v(-16.63, 11.42) * mm, v(-16.5, 11.53) * mm, v(-15.91, 12.03) * mm, v(-15.32, 12.53) * mm]});
            skFitSpline(sketch, "E251", {"points": [v(-11.82, 12.7) * mm, v(-12.08, 13.34) * mm, v(-12.32, 13.86) * mm, v(-12.36, 13.86) * mm]});
            skFitSpline(sketch, "E252", {"points": [v(-12.36, 13.86) * mm, v(-12.4, 13.86) * mm, v(-12.56, 13.75) * mm, v(-12.73, 13.62) * mm]});
            skFitSpline(sketch, "E253", {"points": [v(-12.23, 12.41) * mm, v(-11.8, 11.88) * mm, v(-11.41, 11.47) * mm, v(-11.4, 11.5) * mm]});
            skFitSpline(sketch, "E254", {"points": [v(-11.4, 11.5) * mm, v(-11.37, 11.51) * mm, v(-11.57, 12.05) * mm, v(-11.82, 12.7) * mm]});
            skLineSegment(sketch, "E255", {"start": v(-12.73, 13.62) * mm, "end": v(-13.04, 13.37) * mm});
            skLineSegment(sketch, "E256", {"start": v(-13.04, 13.37) * mm, "end": v(-12.23, 12.41) * mm});
            skFitSpline(sketch, "E257", {"points": [v(-21.27, 13.15) * mm, v(-20.75, 13.57) * mm, v(-20.33, 13.95) * mm, v(-20.32, 14) * mm]});
            skFitSpline(sketch, "E258", {"points": [v(-20.32, 14) * mm, v(-20.32, 14.08) * mm, v(-22.4, 16.56) * mm, v(-22.5, 16.6) * mm]});
            skFitSpline(sketch, "E259", {"points": [v(-22.5, 16.6) * mm, v(-22.55, 16.61) * mm, v(-23.03, 16.25) * mm, v(-23.58, 15.78) * mm]});
            skFitSpline(sketch, "E260", {"points": [v(-23.58, 15.78) * mm, v(-24.12, 15.32) * mm, v(-24.71, 14.83) * mm, v(-24.88, 14.68) * mm]});
            skFitSpline(sketch, "E261", {"points": [v(-22.57, 12.07) * mm, v(-22.37, 12.24) * mm, v(-21.78, 12.72) * mm, v(-21.27, 13.15) * mm]});
            skLineSegment(sketch, "E262", {"start": v(-24.88, 14.68) * mm, "end": v(-25.2, 14.42) * mm});
            skLineSegment(sketch, "E263", {"start": v(-25.2, 14.42) * mm, "end": v(-24.07, 13.1) * mm});
            skLineSegment(sketch, "E264", {"start": v(-24.07, 13.1) * mm, "end": v(-22.94, 11.77) * mm});
            skLineSegment(sketch, "E265", {"start": v(-22.94, 11.77) * mm, "end": v(-22.57, 12.07) * mm});
            skFitSpline(sketch, "E266", {"points": [v(-27.55, 13.52) * mm, v(-26.95, 14.03) * mm, v(-26.43, 14.48) * mm, v(-26.42, 14.52) * mm]});
            skFitSpline(sketch, "E267", {"points": [v(-26.42, 14.52) * mm, v(-26.38, 14.61) * mm, v(-28.5, 17.12) * mm, v(-28.6, 17.12) * mm]});
            skFitSpline(sketch, "E268", {"points": [v(-28.6, 17.12) * mm, v(-28.66, 17.12) * mm, v(-29.27, 16.63) * mm, v(-29.98, 16.03) * mm]});
            skFitSpline(sketch, "E269", {"points": [v(-31.06, 14.7) * mm, v(-30.95, 14.58) * mm, v(-30.44, 13.99) * mm, v(-29.93, 13.4) * mm]});
            skFitSpline(sketch, "E270", {"points": [v(-29.93, 13.4) * mm, v(-29.14, 12.45) * mm, v(-29, 12.33) * mm, v(-28.84, 12.45) * mm]});
            skFitSpline(sketch, "E271", {"points": [v(-28.84, 12.45) * mm, v(-28.74, 12.53) * mm, v(-28.16, 13.01) * mm, v(-27.55, 13.52) * mm]});
            skLineSegment(sketch, "E272", {"start": v(-29.98, 16.03) * mm, "end": v(-31.27, 14.95) * mm});
            skLineSegment(sketch, "E273", {"start": v(-31.27, 14.95) * mm, "end": v(-31.06, 14.7) * mm});
            skFitSpline(sketch, "E274", {"points": [v(-33.83, 13.88) * mm, v(-33.17, 14.43) * mm, v(-32.59, 14.92) * mm, v(-32.53, 14.98) * mm]});
            skFitSpline(sketch, "E275", {"points": [v(-32.53, 14.98) * mm, v(-32.48, 15.03) * mm, v(-32.9, 15.63) * mm, v(-33.52, 16.37) * mm]});
            skFitSpline(sketch, "E276", {"points": [v(-33.52, 16.37) * mm, v(-34.12, 17.09) * mm, v(-34.62, 17.7) * mm, v(-34.63, 17.71) * mm]});
            skFitSpline(sketch, "E277", {"points": [v(-34.63, 17.71) * mm, v(-34.65, 17.74) * mm, v(-35.26, 17.25) * mm, v(-36, 16.63) * mm]});
            skFitSpline(sketch, "E278", {"points": [v(-37.11, 15.23) * mm, v(-36.44, 14.37) * mm, v(-35.16, 12.88) * mm, v(-35.1, 12.88) * mm]});
            skFitSpline(sketch, "E279", {"points": [v(-35.1, 12.88) * mm, v(-35.06, 12.87) * mm, v(-34.48, 13.32) * mm, v(-33.83, 13.88) * mm]});
            skLineSegment(sketch, "E280", {"start": v(-36, 16.63) * mm, "end": v(-37.32, 15.5) * mm});
            skLineSegment(sketch, "E281", {"start": v(-37.32, 15.5) * mm, "end": v(-37.11, 15.23) * mm});
            skFitSpline(sketch, "E282", {"points": [v(-39.95, 14.37) * mm, v(-39.33, 14.9) * mm, v(-38.75, 15.4) * mm, v(-38.66, 15.47) * mm]});
            skFitSpline(sketch, "E283", {"points": [v(-38.66, 15.47) * mm, v(-38.53, 15.6) * mm, v(-38.67, 15.81) * mm, v(-39.59, 16.9) * mm]});
            skFitSpline(sketch, "E284", {"points": [v(-39.59, 16.9) * mm, v(-40.18, 17.6) * mm, v(-40.7, 18.2) * mm, v(-40.74, 18.22) * mm]});
            skFitSpline(sketch, "E285", {"points": [v(-40.74, 18.22) * mm, v(-40.79, 18.25) * mm, v(-41.07, 18.07) * mm, v(-41.37, 17.82) * mm]});
            skFitSpline(sketch, "E286", {"points": [v(-41.37, 17.82) * mm, v(-41.99, 17.3) * mm, v(-41.98, 17.33) * mm, v(-41.68, 15.3) * mm]});
            skFitSpline(sketch, "E287", {"points": [v(-41.68, 15.3) * mm, v(-41.5, 14.06) * mm, v(-41.33, 13.42) * mm, v(-41.18, 13.42) * mm]});
            skFitSpline(sketch, "E288", {"points": [v(-41.18, 13.42) * mm, v(-41.13, 13.42) * mm, v(-40.57, 13.85) * mm, v(-39.95, 14.37) * mm]});
            skFitSpline(sketch, "E289", {"points": [v(-13.11, 15.4) * mm, v(-13.34, 15.8) * mm, v(-13.75, 16.5) * mm, v(-14.03, 16.94) * mm]});
            skLineSegment(sketch, "E290", {"start": v(-13.09, 14.38) * mm, "end": v(-12.71, 14.68) * mm});
            skLineSegment(sketch, "E291", {"start": v(-12.71, 14.68) * mm, "end": v(-13.11, 15.4) * mm});
            skFitSpline(sketch, "E292", {"points": [v(-15.14, 17.23) * mm, v(-15.47, 16.95) * mm, v(-15.72, 16.67) * mm, v(-15.7, 16.62) * mm]});
            skFitSpline(sketch, "E293", {"points": [v(-15.7, 16.62) * mm, v(-15.66, 16.46) * mm, v(-13.64, 14.09) * mm, v(-13.55, 14.09) * mm]});
            skFitSpline(sketch, "E294", {"points": [v(-13.55, 14.09) * mm, v(-13.5, 14.09) * mm, v(-13.3, 14.22) * mm, v(-13.09, 14.38) * mm]});
            skLineSegment(sketch, "E295", {"start": v(-14.03, 16.94) * mm, "end": v(-14.54, 17.74) * mm});
            skLineSegment(sketch, "E296", {"start": v(-14.54, 17.74) * mm, "end": v(-15.14, 17.23) * mm});
            skFitSpline(sketch, "E297", {"points": [v(-18.08, 15.85) * mm, v(-17.43, 16.4) * mm, v(-17.04, 16.8) * mm, v(-17.08, 16.88) * mm]});
            skFitSpline(sketch, "E298", {"points": [v(-17.08, 16.88) * mm, v(-17.23, 17.13) * mm, v(-19.16, 19.39) * mm, v(-19.22, 19.39) * mm]});
            skFitSpline(sketch, "E299", {"points": [v(-19.22, 19.39) * mm, v(-19.27, 19.39) * mm, v(-21.58, 17.49) * mm, v(-21.85, 17.23) * mm]});
            skFitSpline(sketch, "E300", {"points": [v(-21.85, 17.23) * mm, v(-21.87, 17.2) * mm, v(-21.38, 16.6) * mm, v(-20.75, 15.86) * mm]});
            skFitSpline(sketch, "E301", {"points": [v(-20.75, 15.86) * mm, v(-19.63, 14.53) * mm, v(-19.62, 14.52) * mm, v(-19.4, 14.73) * mm]});
            skFitSpline(sketch, "E302", {"points": [v(-19.4, 14.73) * mm, v(-19.26, 14.84) * mm, v(-18.67, 15.34) * mm, v(-18.08, 15.85) * mm]});
            skFitSpline(sketch, "E303", {"points": [v(-24.03, 16.46) * mm, v(-23.51, 16.89) * mm, v(-23.09, 17.26) * mm, v(-23.09, 17.3) * mm]});
            skFitSpline(sketch, "E304", {"points": [v(-23.09, 17.3) * mm, v(-23.08, 17.4) * mm, v(-25.2, 19.88) * mm, v(-25.3, 19.88) * mm]});
            skFitSpline(sketch, "E305", {"points": [v(-25.3, 19.88) * mm, v(-25.44, 19.88) * mm, v(-27.93, 17.8) * mm, v(-27.9, 17.7) * mm]});
            skFitSpline(sketch, "E306", {"points": [v(-27.9, 17.7) * mm, v(-27.9, 17.67) * mm, v(-27.4, 17.06) * mm, v(-26.8, 16.35) * mm]});
            skFitSpline(sketch, "E307", {"points": [v(-25.34, 15.38) * mm, v(-25.14, 15.55) * mm, v(-24.55, 16.03) * mm, v(-24.03, 16.46) * mm]});
            skLineSegment(sketch, "E308", {"start": v(-26.8, 16.35) * mm, "end": v(-25.71, 15.07) * mm});
            skLineSegment(sketch, "E309", {"start": v(-25.71, 15.07) * mm, "end": v(-25.34, 15.38) * mm});
            skFitSpline(sketch, "E310", {"points": [v(-30.48, 16.7) * mm, v(-29.78, 17.28) * mm, v(-29.2, 17.8) * mm, v(-29.2, 17.85) * mm]});
            skFitSpline(sketch, "E311", {"points": [v(-29.2, 17.85) * mm, v(-29.2, 17.9) * mm, v(-29.66, 18.47) * mm, v(-30.2, 19.12) * mm]});
            skFitSpline(sketch, "E312", {"points": [v(-30.2, 19.12) * mm, v(-30.75, 19.77) * mm, v(-31.23, 20.35) * mm, v(-31.27, 20.41) * mm]});
            skFitSpline(sketch, "E313", {"points": [v(-31.27, 20.41) * mm, v(-31.33, 20.51) * mm, v(-33.53, 18.79) * mm, v(-33.88, 18.37) * mm]});
            skFitSpline(sketch, "E314", {"points": [v(-33.88, 18.37) * mm, v(-33.97, 18.25) * mm, v(-33.76, 17.94) * mm, v(-32.93, 16.93) * mm]});
            skFitSpline(sketch, "E315", {"points": [v(-32.93, 16.93) * mm, v(-32.34, 16.22) * mm, v(-31.83, 15.64) * mm, v(-31.8, 15.64) * mm]});
            skFitSpline(sketch, "E316", {"points": [v(-31.8, 15.64) * mm, v(-31.77, 15.63) * mm, v(-31.17, 16.11) * mm, v(-30.48, 16.7) * mm]});
            skFitSpline(sketch, "E317", {"points": [v(-36.6, 17.19) * mm, v(-35.93, 17.74) * mm, v(-35.35, 18.24) * mm, v(-35.3, 18.29) * mm]});
            skFitSpline(sketch, "E318", {"points": [v(-35.3, 18.29) * mm, v(-35.21, 18.36) * mm, v(-37.16, 20.82) * mm, v(-37.44, 20.99) * mm]});
            skFitSpline(sketch, "E319", {"points": [v(-37.44, 20.99) * mm, v(-37.56, 21.06) * mm, v(-40.1, 18.93) * mm, v(-40.06, 18.8) * mm]});
            skFitSpline(sketch, "E320", {"points": [v(-40.06, 18.8) * mm, v(-40, 18.64) * mm, v(-37.94, 16.19) * mm, v(-37.86, 16.19) * mm]});
            skFitSpline(sketch, "E321", {"points": [v(-37.86, 16.19) * mm, v(-37.82, 16.18) * mm, v(-37.25, 16.64) * mm, v(-36.6, 17.19) * mm]});
            skFitSpline(sketch, "E322", {"points": [v(-15.1, 18.55) * mm, v(-15.9, 19.59) * mm, v(-16.71, 20.6) * mm, v(-16.94, 20.81) * mm]});
            skFitSpline(sketch, "E323", {"points": [v(-16.94, 20.81) * mm, v(-17.26, 21.1) * mm, v(-17.3, 21.1) * mm, v(-18.15, 20.34) * mm]});
            skFitSpline(sketch, "E324", {"points": [v(-15.67, 17.86) * mm, v(-15.26, 18.22) * mm, v(-15.05, 18.47) * mm, v(-15.1, 18.55) * mm]});
            skLineSegment(sketch, "E325", {"start": v(-18.15, 20.34) * mm, "end": v(-18.58, 19.97) * mm});
            skLineSegment(sketch, "E326", {"start": v(-18.58, 19.97) * mm, "end": v(-17.45, 18.63) * mm});
            skLineSegment(sketch, "E327", {"start": v(-17.45, 18.63) * mm, "end": v(-16.32, 17.3) * mm});
            skLineSegment(sketch, "E328", {"start": v(-16.32, 17.3) * mm, "end": v(-15.67, 17.86) * mm});
            skFitSpline(sketch, "E329", {"points": [v(-19.9, 20.25) * mm, v(-20.3, 20.76) * mm, v(-21.9, 22.65) * mm, v(-21.97, 22.67) * mm]});
            skFitSpline(sketch, "E330", {"points": [v(-21.97, 22.67) * mm, v(-22.06, 22.71) * mm, v(-24.57, 20.6) * mm, v(-24.57, 20.5) * mm]});
            skFitSpline(sketch, "E331", {"points": [v(-24.57, 20.5) * mm, v(-24.57, 20.44) * mm, v(-24.08, 19.83) * mm, v(-23.49, 19.12) * mm]});
            skFitSpline(sketch, "E332", {"points": [v(-21.08, 18.95) * mm, v(-19.92, 19.93) * mm, v(-19.77, 20.1) * mm, v(-19.9, 20.25) * mm]});
            skLineSegment(sketch, "E333", {"start": v(-23.49, 19.12) * mm, "end": v(-22.4, 17.84) * mm});
            skLineSegment(sketch, "E334", {"start": v(-22.4, 17.84) * mm, "end": v(-21.08, 18.95) * mm});
            skFitSpline(sketch, "E335", {"points": [v(-27.12, 19.5) * mm, v(-26.43, 20.07) * mm, v(-25.86, 20.58) * mm, v(-25.88, 20.63) * mm]});
            skFitSpline(sketch, "E336", {"points": [v(-25.88, 20.63) * mm, v(-25.92, 20.79) * mm, v(-28, 23.24) * mm, v(-28.08, 23.22) * mm]});
            skFitSpline(sketch, "E337", {"points": [v(-28.08, 23.22) * mm, v(-28.24, 23.18) * mm, v(-30.69, 21.1) * mm, v(-30.67, 21.02) * mm]});
            skFitSpline(sketch, "E338", {"points": [v(-30.67, 21.02) * mm, v(-30.62, 20.85) * mm, v(-28.54, 18.4) * mm, v(-28.47, 18.43) * mm]});
            skFitSpline(sketch, "E339", {"points": [v(-28.47, 18.43) * mm, v(-28.42, 18.44) * mm, v(-27.82, 18.92) * mm, v(-27.12, 19.5) * mm]});
            skFitSpline(sketch, "E340", {"points": [v(-41.9, 19.16) * mm, v(-42.04, 18.43) * mm, v(-41.95, 18.33) * mm, v(-41.54, 18.76) * mm]});
            skLineSegment(sketch, "E341", {"start": v(-41.54, 18.76) * mm, "end": v(-41.3, 19.02) * mm});
            skLineSegment(sketch, "E342", {"start": v(-41.3, 19.02) * mm, "end": v(-41.56, 19.26) * mm});
            skLineSegment(sketch, "E343", {"start": v(-41.56, 19.26) * mm, "end": v(-41.82, 19.5) * mm});
            skLineSegment(sketch, "E344", {"start": v(-41.82, 19.5) * mm, "end": v(-41.9, 19.16) * mm});
            skFitSpline(sketch, "E345", {"points": [v(-33.24, 20) * mm, v(-32.54, 20.6) * mm, v(-31.95, 21.09) * mm, v(-31.93, 21.1) * mm]});
            skFitSpline(sketch, "E346", {"points": [v(-31.93, 21.1) * mm, v(-31.88, 21.15) * mm, v(-33.97, 23.65) * mm, v(-34.13, 23.75) * mm]});
            skFitSpline(sketch, "E347", {"points": [v(-34.13, 23.75) * mm, v(-34.26, 23.83) * mm, v(-36.8, 21.71) * mm, v(-36.75, 21.57) * mm]});
            skFitSpline(sketch, "E348", {"points": [v(-36.75, 21.57) * mm, v(-36.7, 21.42) * mm, v(-34.64, 18.95) * mm, v(-34.56, 18.95) * mm]});
            skFitSpline(sketch, "E349", {"points": [v(-34.56, 18.95) * mm, v(-34.53, 18.95) * mm, v(-33.93, 19.42) * mm, v(-33.24, 20) * mm]});
            skFitSpline(sketch, "E350", {"points": [v(-39.29, 20.64) * mm, v(-38.63, 21.19) * mm, v(-38.1, 21.67) * mm, v(-38.1, 21.73) * mm]});
            skFitSpline(sketch, "E351", {"points": [v(-38.1, 21.73) * mm, v(-38.1, 21.78) * mm, v(-38.58, 22.4) * mm, v(-39.17, 23.1) * mm]});
            skFitSpline(sketch, "E352", {"points": [v(-40.6, 23.74) * mm, v(-40.98, 23.06) * mm, v(-41.63, 21.22) * mm, v(-41.63, 20.82) * mm]});
            skFitSpline(sketch, "E353", {"points": [v(-41.63, 20.82) * mm, v(-41.63, 20.53) * mm, v(-40.75, 19.48) * mm, v(-40.59, 19.58) * mm]});
            skFitSpline(sketch, "E354", {"points": [v(-40.59, 19.58) * mm, v(-40.53, 19.62) * mm, v(-39.94, 20.1) * mm, v(-39.29, 20.64) * mm]});
            skLineSegment(sketch, "E355", {"start": v(-39.17, 23.1) * mm, "end": v(-40.23, 24.37) * mm});
            skLineSegment(sketch, "E356", {"start": v(-40.23, 24.37) * mm, "end": v(-40.6, 23.74) * mm});
            skFitSpline(sketch, "E357", {"points": [v(-18.13, 22.13) * mm, v(-18.33, 22.33) * mm, v(-18.91, 22.87) * mm, v(-19.42, 23.32) * mm]});
            skFitSpline(sketch, "E358", {"points": [v(-20.83, 23.72) * mm, v(-21.1, 23.5) * mm, v(-21.3, 23.28) * mm, v(-21.29, 23.24) * mm]});
            skFitSpline(sketch, "E359", {"points": [v(-21.29, 23.24) * mm, v(-21.27, 23.2) * mm, v(-20.77, 22.58) * mm, v(-20.17, 21.88) * mm]});
            skLineSegment(sketch, "E360", {"start": v(-19.42, 23.32) * mm, "end": v(-20.34, 24.13) * mm});
            skLineSegment(sketch, "E361", {"start": v(-20.34, 24.13) * mm, "end": v(-20.83, 23.72) * mm});
            skLineSegment(sketch, "E362", {"start": v(-20.17, 21.88) * mm, "end": v(-19.09, 20.6) * mm});
            skLineSegment(sketch, "E363", {"start": v(-19.09, 20.6) * mm, "end": v(-18.43, 21.17) * mm});
            skLineSegment(sketch, "E364", {"start": v(-18.43, 21.17) * mm, "end": v(-17.77, 21.74) * mm});
            skLineSegment(sketch, "E365", {"start": v(-17.77, 21.74) * mm, "end": v(-18.13, 22.13) * mm});
            skFitSpline(sketch, "E366", {"points": [v(-22.77, 23.7) * mm, v(-23.46, 24.55) * mm, v(-24.69, 26) * mm, v(-24.74, 26) * mm]});
            skFitSpline(sketch, "E367", {"points": [v(-24.74, 26) * mm, v(-24.85, 26.02) * mm, v(-27.33, 23.91) * mm, v(-27.33, 23.8) * mm]});
            skFitSpline(sketch, "E368", {"points": [v(-27.33, 23.8) * mm, v(-27.33, 23.72) * mm, v(-25.29, 21.18) * mm, v(-25.2, 21.16) * mm]});
            skFitSpline(sketch, "E369", {"points": [v(-25.2, 21.16) * mm, v(-25.18, 21.16) * mm, v(-24.57, 21.65) * mm, v(-23.84, 22.27) * mm]});
            skLineSegment(sketch, "E370", {"start": v(-23.84, 22.27) * mm, "end": v(-22.52, 23.38) * mm});
            skLineSegment(sketch, "E371", {"start": v(-22.52, 23.38) * mm, "end": v(-22.77, 23.7) * mm});
            skFitSpline(sketch, "E372", {"points": [v(-29.94, 22.77) * mm, v(-29.23, 23.36) * mm, v(-28.64, 23.86) * mm, v(-28.62, 23.87) * mm]});
            skFitSpline(sketch, "E373", {"points": [v(-28.62, 23.87) * mm, v(-28.57, 23.9) * mm, v(-30.67, 26.42) * mm, v(-30.83, 26.52) * mm]});
            skFitSpline(sketch, "E374", {"points": [v(-30.83, 26.52) * mm, v(-30.96, 26.6) * mm, v(-33.48, 24.48) * mm, v(-33.43, 24.33) * mm]});
            skFitSpline(sketch, "E375", {"points": [v(-33.43, 24.33) * mm, v(-33.4, 24.2) * mm, v(-31.33, 21.71) * mm, v(-31.27, 21.7) * mm]});
            skFitSpline(sketch, "E376", {"points": [v(-31.27, 21.7) * mm, v(-31.24, 21.7) * mm, v(-30.65, 22.19) * mm, v(-29.94, 22.77) * mm]});
            skFitSpline(sketch, "E377", {"points": [v(-36.02, 23.38) * mm, v(-35.37, 23.93) * mm, v(-34.82, 24.42) * mm, v(-34.8, 24.48) * mm]});
            skFitSpline(sketch, "E378", {"points": [v(-34.8, 24.48) * mm, v(-34.78, 24.54) * mm, v(-35.28, 25.2) * mm, v(-35.9, 25.93) * mm]});
            skFitSpline(sketch, "E379", {"points": [v(-35.9, 25.93) * mm, v(-36.52, 26.68) * mm, v(-37.05, 27.3) * mm, v(-37.06, 27.32) * mm]});
            skFitSpline(sketch, "E380", {"points": [v(-37.06, 27.32) * mm, v(-37.17, 27.47) * mm, v(-38.76, 26.22) * mm, v(-39.33, 25.54) * mm]});
            skFitSpline(sketch, "E381", {"points": [v(-38.57, 23.66) * mm, v(-37.93, 22.9) * mm, v(-37.36, 22.3) * mm, v(-37.3, 22.32) * mm]});
            skFitSpline(sketch, "E382", {"points": [v(-37.3, 22.32) * mm, v(-37.25, 22.36) * mm, v(-36.68, 22.83) * mm, v(-36.02, 23.38) * mm]});
            skLineSegment(sketch, "E383", {"start": v(-39.33, 25.54) * mm, "end": v(-39.73, 25.06) * mm});
            skLineSegment(sketch, "E384", {"start": v(-39.73, 25.06) * mm, "end": v(-38.57, 23.66) * mm});
            skFitSpline(sketch, "E385", {"points": [v(-21.55, 25.02) * mm, v(-22.2, 25.5) * mm, v(-23.98, 26.59) * mm, v(-24.02, 26.54) * mm]});
            skFitSpline(sketch, "E386", {"points": [v(-24.02, 26.54) * mm, v(-24.04, 26.52) * mm, v(-23.58, 25.93) * mm, v(-22.99, 25.23) * mm]});
            skFitSpline(sketch, "E387", {"points": [v(-22.99, 25.23) * mm, v(-21.85, 23.86) * mm, v(-21.83, 23.85) * mm, v(-21.33, 24.4) * mm]});
            skLineSegment(sketch, "E388", {"start": v(-21.33, 24.4) * mm, "end": v(-21.07, 24.67) * mm});
            skLineSegment(sketch, "E389", {"start": v(-21.07, 24.67) * mm, "end": v(-21.55, 25.02) * mm});
            skFitSpline(sketch, "E390", {"points": [v(-25.63, 27.12) * mm, v(-25.93, 27.5) * mm, v(-26.13, 27.6) * mm, v(-27.19, 27.94) * mm]});
            skFitSpline(sketch, "E391", {"points": [v(-27.19, 27.94) * mm, v(-27.85, 28.15) * mm, v(-28.5, 28.33) * mm, v(-28.62, 28.33) * mm]});
            skFitSpline(sketch, "E392", {"points": [v(-28.62, 28.33) * mm, v(-28.8, 28.33) * mm, v(-29.97, 27.48) * mm, v(-30.15, 27.2) * mm]});
            skFitSpline(sketch, "E393", {"points": [v(-30.15, 27.2) * mm, v(-30.2, 27.14) * mm, v(-28.06, 24.48) * mm, v(-27.96, 24.47) * mm]});
            skFitSpline(sketch, "E394", {"points": [v(-27.96, 24.47) * mm, v(-27.94, 24.47) * mm, v(-27.33, 24.97) * mm, v(-26.6, 25.58) * mm]});
            skLineSegment(sketch, "E395", {"start": v(-26.6, 25.58) * mm, "end": v(-25.29, 26.69) * mm});
            skLineSegment(sketch, "E396", {"start": v(-25.29, 26.69) * mm, "end": v(-25.63, 27.12) * mm});
            skFitSpline(sketch, "E397", {"points": [v(-32.63, 26.23) * mm, v(-32.03, 26.73) * mm, v(-31.51, 27.19) * mm, v(-31.5, 27.24) * mm]});
            skFitSpline(sketch, "E398", {"points": [v(-31.5, 27.24) * mm, v(-31.47, 27.3) * mm, v(-31.7, 27.63) * mm, v(-31.99, 28) * mm]});
            skFitSpline(sketch, "E399", {"points": [v(-31.99, 28) * mm, v(-32.49, 28.6) * mm, v(-32.55, 28.65) * mm, v(-33, 28.66) * mm]});
            skFitSpline(sketch, "E400", {"points": [v(-33, 28.66) * mm, v(-33.26, 28.66) * mm, v(-33.7, 28.6) * mm, v(-34, 28.54) * mm]});
            skFitSpline(sketch, "E401", {"points": [v(-34, 28.54) * mm, v(-34.77, 28.36) * mm, v(-36.21, 27.88) * mm, v(-36.27, 27.79) * mm]});
            skFitSpline(sketch, "E402", {"points": [v(-36.27, 27.79) * mm, v(-36.3, 27.74) * mm, v(-35.82, 27.1) * mm, v(-35.2, 26.37) * mm]});
            skFitSpline(sketch, "E403", {"points": [v(-35.2, 26.37) * mm, v(-34.23, 25.21) * mm, v(-34.05, 25.05) * mm, v(-33.9, 25.17) * mm]});
            skFitSpline(sketch, "E404", {"points": [v(-33.9, 25.17) * mm, v(-33.81, 25.25) * mm, v(-33.24, 25.73) * mm, v(-32.63, 26.23) * mm]});
            skFitSpline(sketch, "E405", {"points": [v(-29.93, 28.56) * mm, v(-29.93, 28.63) * mm, v(-31.38, 28.79) * mm, v(-31.46, 28.72) * mm]});
            skFitSpline(sketch, "E406", {"points": [v(-31.46, 28.72) * mm, v(-31.48, 28.7) * mm, v(-31.33, 28.48) * mm, v(-31.14, 28.23) * mm]});
            skFitSpline(sketch, "E407", {"points": [v(-30.35, 28.14) * mm, v(-30.12, 28.32) * mm, v(-29.93, 28.51) * mm, v(-29.93, 28.56) * mm]});
            skLineSegment(sketch, "E408", {"start": v(-31.14, 28.23) * mm, "end": v(-30.78, 27.8) * mm});
            skLineSegment(sketch, "E409", {"start": v(-30.78, 27.8) * mm, "end": v(-30.35, 28.14) * mm});
            skFitSpline(sketch, "E410", {"points": [v(-29.93, 28.56) * mm, v(-28.62, 28.33) * mm], "startDerivative": vector(1.3, -0.22) * mm, "endDerivative": vector(1.3, -0.22) * mm});
            skFitSpline(sketch, "E411", {"points": [v(-37.06, 27.32) * mm, v(-36.27, 27.79) * mm], "startDerivative": vector(0.79, 0.47) * mm, "endDerivative": vector(0.79, 0.47) * mm});
            skFitSpline(sketch, "E412", {"points": [v(-40.23, 24.37) * mm, v(-39.73, 25.06) * mm], "startDerivative": vector(0.5, 0.69) * mm, "endDerivative": vector(0.5, 0.69) * mm});
            skSolve(sketch);
        }
        {
            var Q0;
            Q0 = qSketchRegion(id + "F0", true);
            extrude(context, id + "F1", {"entities" : qUnion([Q0]), "depth" : 3.8 * mm, "offsetDistance" : 25.4 * mm});
        }
        {
            var Q0;
            Q0=qCreatedBy(makeId("Front.planeOp"),FACE);
            var sketch = newSketch(context, id + "F2", { "sketchPlane" : qUnion([Q0])});
            skFitSpline(sketch, "E413", {"points": [v(8.3, -34.6) * mm, v(7.75, -33.92) * mm, v(7.73, -33.88) * mm, v(7.73, -33.21) * mm]});
            skFitSpline(sketch, "E414", {"points": [v(0.8, -24.26) * mm, v(-3.02, -19.72) * mm, v(-6.18, -15.94) * mm, v(-6.23, -15.86) * mm]});
            skFitSpline(sketch, "E415", {"points": [v(-6.23, -15.86) * mm, v(-6.27, -15.78) * mm, v(-6.25, -15.65) * mm, v(-6.18, -15.57) * mm]});
            skFitSpline(sketch, "E416", {"points": [v(-6.18, -15.57) * mm, v(-6.11, -15.48) * mm, v(-6.09, -15.36) * mm, v(-6.12, -15.3) * mm]});
            skFitSpline(sketch, "E417", {"points": [v(-6.12, -15.3) * mm, v(-6.22, -15.14) * mm, v(-8.37, -13.48) * mm, v(-9.44, -12.74) * mm]});
            skFitSpline(sketch, "E418", {"points": [v(-9.44, -12.74) * mm, v(-12.31, -10.75) * mm, v(-14.7, -9.72) * mm, v(-21.08, -7.72) * mm]});
            skFitSpline(sketch, "E419", {"points": [v(-21.08, -7.72) * mm, v(-22.32, -7.33) * mm, v(-23.37, -6.97) * mm, v(-23.4, -6.91) * mm]});
            skFitSpline(sketch, "E420", {"points": [v(-23.4, -6.91) * mm, v(-23.44, -6.86) * mm, v(-23.84, -6.7) * mm, v(-24.3, -6.57) * mm]});
            skFitSpline(sketch, "E421", {"points": [v(-24.3, -6.57) * mm, v(-28.9, -5.24) * mm, v(-33.33, -2.3) * mm, v(-37.04, 1.88) * mm]});
            skFitSpline(sketch, "E422", {"points": [v(-37.04, 1.88) * mm, v(-41.78, 7.22) * mm, v(-44.33, 13.72) * mm, v(-43.87, 19.25) * mm]});
            skFitSpline(sketch, "E423", {"points": [v(-43.87, 19.25) * mm, v(-43.53, 23.3) * mm, v(-41.98, 26.27) * mm, v(-39.04, 28.52) * mm]});
            skFitSpline(sketch, "E424", {"points": [v(-39.04, 28.52) * mm, v(-37.1, 30) * mm, v(-33.96, 30.88) * mm, v(-31.18, 30.72) * mm]});
            skFitSpline(sketch, "E425", {"points": [v(-31.18, 30.72) * mm, v(-28.5, 30.57) * mm, v(-26.4, 29.98) * mm, v(-23.61, 28.6) * mm]});
            skFitSpline(sketch, "E426", {"points": [v(-23.61, 28.6) * mm, v(-15.7, 24.66) * mm, v(-9.26, 15.6) * mm, v(-8.28, 7.03) * mm]});
            skFitSpline(sketch, "E427", {"points": [v(-8.28, 7.03) * mm, v(-8.22, 6.51) * mm, v(-8.13, 6.07) * mm, v(-8.08, 6.03) * mm]});
            skFitSpline(sketch, "E428", {"points": [v(-8.08, 6.03) * mm, v(-8.02, 6) * mm, v(-7.85, 4.93) * mm, v(-7.68, 3.65) * mm]});
            skFitSpline(sketch, "E429", {"points": [v(-7.68, 3.65) * mm, v(-7.3, 0.68) * mm, v(-6.69, -2.97) * mm, v(-6.3, -4.53) * mm]});
            skFitSpline(sketch, "E430", {"points": [v(-6.3, -4.53) * mm, v(-5.88, -6.16) * mm, v(-5.03, -8.3) * mm, v(-3.9, -10.52) * mm]});
            skFitSpline(sketch, "E431", {"points": [v(-3.9, -10.52) * mm, v(-2.82, -12.66) * mm, v(-2.8, -12.7) * mm, v(-2.57, -12.5) * mm]});
            skFitSpline(sketch, "E432", {"points": [v(-2.57, -12.5) * mm, v(-2.47, -12.42) * mm, v(-2.39, -12.42) * mm, v(-2.34, -12.49) * mm]});
            skFitSpline(sketch, "E433", {"points": [v(-2.34, -12.49) * mm, v(-2.3, -12.55) * mm, v(0.81, -16.27) * mm, v(4.58, -20.75) * mm]});
            skFitSpline(sketch, "E434", {"points": [v(4.58, -20.75) * mm, v(8.42, -25.33) * mm, v(11.53, -28.94) * mm, v(11.68, -29) * mm]});
            skFitSpline(sketch, "E435", {"points": [v(11.68, -29) * mm, v(11.82, -29.05) * mm, v(12.19, -29.1) * mm, v(12.48, -29.1) * mm]});
            skFitSpline(sketch, "E436", {"points": [v(12.48, -29.1) * mm, v(13.02, -29.1) * mm, v(13.03, -29.1) * mm, v(13.7, -29.89) * mm]});
            skFitSpline(sketch, "E437", {"points": [v(13.7, -29.89) * mm, v(14.06, -30.33) * mm, v(14.32, -30.72) * mm, v(14.28, -30.76) * mm]});
            skFitSpline(sketch, "E438", {"points": [v(14.28, -30.76) * mm, v(14.23, -30.8) * mm, v(13.1, -31.74) * mm, v(11.76, -32.85) * mm]});
            skFitSpline(sketch, "E439", {"points": [v(11.76, -32.85) * mm, v(10.43, -33.96) * mm, v(9.23, -34.97) * mm, v(9.1, -35.08) * mm]});
            skFitSpline(sketch, "E440", {"points": [v(9.1, -35.08) * mm, v(8.87, -35.29) * mm, v(8.86, -35.28) * mm, v(8.3, -34.6) * mm]});
            skLineSegment(sketch, "E441", {"start": v(7.73, -33.21) * mm, "end": v(7.73, -32.53) * mm});
            skLineSegment(sketch, "E442", {"start": v(7.73, -32.53) * mm, "end": v(0.8, -24.26) * mm});
            skLineSegment(sketch, "E443", {"start": v(0.8, -24.26) * mm, "end": v(7.73, -33.21) * mm});
            skFitSpline(sketch, "E444", {"points": [v(-5.17, -12.46) * mm, v(-7.27, -8.56) * mm, v(-8.18, -6.01) * mm, v(-8.85, -2.18) * mm]});
            skFitSpline(sketch, "E445", {"points": [v(-8.85, -2.18) * mm, v(-9, -1.37) * mm, v(-9.14, -0.71) * mm, v(-9.18, -0.71) * mm]});
            skFitSpline(sketch, "E446", {"points": [v(-9.18, -0.71) * mm, v(-9.22, -0.71) * mm, v(-9.3, -0.87) * mm, v(-9.38, -1.07) * mm]});
            skFitSpline(sketch, "E447", {"points": [v(-9.38, -1.07) * mm, v(-9.55, -1.57) * mm, v(-10.2, -2.63) * mm, v(-10.85, -3.45) * mm]});
            skFitSpline(sketch, "E448", {"points": [v(-10.85, -3.45) * mm, v(-11.95, -4.84) * mm, v(-14.11, -6.26) * mm, v(-15.87, -6.74) * mm]});
            skFitSpline(sketch, "E449", {"points": [v(-15.87, -6.74) * mm, v(-16.25, -6.85) * mm, v(-16.56, -6.96) * mm, v(-16.56, -7) * mm]});
            skFitSpline(sketch, "E450", {"points": [v(-16.56, -7) * mm, v(-16.56, -7.04) * mm, v(-15.9, -7.31) * mm, v(-15.1, -7.6) * mm]});
            skFitSpline(sketch, "E451", {"points": [v(-15.1, -7.6) * mm, v(-12.95, -8.4) * mm, v(-11.63, -9) * mm, v(-10.26, -9.82) * mm]});
            skFitSpline(sketch, "E452", {"points": [v(-10.26, -9.82) * mm, v(-8.87, -10.66) * mm, v(-6.9, -12.03) * mm, v(-5.48, -13.18) * mm]});
            skFitSpline(sketch, "E453", {"points": [v(-5.48, -13.18) * mm, v(-4.94, -13.61) * mm, v(-4.47, -13.95) * mm, v(-4.45, -13.92) * mm]});
            skFitSpline(sketch, "E454", {"points": [v(-4.45, -13.92) * mm, v(-4.42, -13.9) * mm, v(-4.75, -13.24) * mm, v(-5.17, -12.46) * mm]});
            skFitSpline(sketch, "E455", {"points": [v(-17.72, -5.12) * mm, v(-17.36, -5.06) * mm, v(-16.8, -4.93) * mm, v(-16.48, -4.84) * mm]});
            skFitSpline(sketch, "E456", {"points": [v(-16.48, -4.84) * mm, v(-15.96, -4.69) * mm, v(-15.9, -4.65) * mm, v(-16.03, -4.49) * mm]});
            skFitSpline(sketch, "E457", {"points": [v(-16.03, -4.49) * mm, v(-16.41, -4) * mm, v(-18.04, -2.1) * mm, v(-18.07, -2.1) * mm]});
            skFitSpline(sketch, "E458", {"points": [v(-18.07, -2.1) * mm, v(-18.1, -2.1) * mm, v(-18.7, -2.59) * mm, v(-19.42, -3.2) * mm]});
            skFitSpline(sketch, "E459", {"points": [v(-19.14, -5.27) * mm, v(-18.73, -5.25) * mm, v(-18.09, -5.18) * mm, v(-17.72, -5.12) * mm]});
            skLineSegment(sketch, "E460", {"start": v(-19.42, -3.2) * mm, "end": v(-20.74, -4.3) * mm});
            skLineSegment(sketch, "E461", {"start": v(-20.74, -4.3) * mm, "end": v(-20.32, -4.8) * mm});
            skLineSegment(sketch, "E462", {"start": v(-20.32, -4.8) * mm, "end": v(-19.9, -5.3) * mm});
            skLineSegment(sketch, "E463", {"start": v(-19.9, -5.3) * mm, "end": v(-19.14, -5.27) * mm});
            skLineSegment(sketch, "E464", {"start": v(-19.14, -5.27) * mm, "end": v(-19.42, -3.2) * mm});
            skFitSpline(sketch, "E465", {"points": [v(-21.2, -5.01) * mm, v(-21.3, -4.82) * mm, v(-21.36, -4.8) * mm, v(-21.5, -4.92) * mm]});
            skFitSpline(sketch, "E466", {"points": [v(-21.5, -4.92) * mm, v(-21.65, -5.05) * mm, v(-21.64, -5.07) * mm, v(-21.46, -5.14) * mm]});
            skFitSpline(sketch, "E467", {"points": [v(-21.46, -5.14) * mm, v(-21.13, -5.28) * mm, v(-21.08, -5.25) * mm, v(-21.2, -5.01) * mm]});
            skFitSpline(sketch, "E468", {"points": [v(-22.33, -4.57) * mm, v(-22.12, -4.38) * mm, v(-21.98, -4.17) * mm, v(-22.01, -4.1) * mm]});
            skFitSpline(sketch, "E469", {"points": [v(-22.01, -4.1) * mm, v(-22.04, -4.03) * mm, v(-22.52, -3.43) * mm, v(-23.08, -2.78) * mm]});
            skFitSpline(sketch, "E470", {"points": [v(-23.08, -2.78) * mm, v(-24, -1.7) * mm, v(-24.12, -1.6) * mm, v(-24.3, -1.73) * mm]});
            skFitSpline(sketch, "E471", {"points": [v(-24.3, -1.73) * mm, v(-24.73, -2.04) * mm, v(-26.5, -3.53) * mm, v(-26.5, -3.6) * mm]});
            skFitSpline(sketch, "E472", {"points": [v(-26.5, -3.6) * mm, v(-26.51, -3.74) * mm, v(-23.33, -4.88) * mm, v(-22.86, -4.9) * mm]});
            skFitSpline(sketch, "E473", {"points": [v(-22.86, -4.9) * mm, v(-22.77, -4.9) * mm, v(-22.53, -4.75) * mm, v(-22.33, -4.57) * mm]});
            skFitSpline(sketch, "E474", {"points": [v(-14.12, -3.7) * mm, v(-13.67, -3.4) * mm, v(-13.08, -2.93) * mm, v(-12.82, -2.65) * mm]});
            skFitSpline(sketch, "E475", {"points": [v(-12.88, -1.5) * mm, v(-14.17, 0.02) * mm, v(-14.69, 0.62) * mm, v(-14.75, 0.64) * mm]});
            skFitSpline(sketch, "E476", {"points": [v(-14.75, 0.64) * mm, v(-14.78, 0.66) * mm, v(-15.4, 0.18) * mm, v(-16.13, -0.42) * mm]});
            skLineSegment(sketch, "E477", {"start": v(-12.82, -2.65) * mm, "end": v(-12.35, -2.14) * mm});
            skLineSegment(sketch, "E478", {"start": v(-12.35, -2.14) * mm, "end": v(-12.88, -1.5) * mm});
            skLineSegment(sketch, "E479", {"start": v(-12.88, -1.5) * mm, "end": v(-12.82, -2.65) * mm});
            skFitSpline(sketch, "E480", {"points": [v(-16.92, -2.14) * mm, v(-16.63, -2.48) * mm, v(-16.13, -3.1) * mm, v(-15.8, -3.5) * mm]});
            skFitSpline(sketch, "E481", {"points": [v(-15.8, -3.5) * mm, v(-15.46, -3.9) * mm, v(-15.13, -4.23) * mm, v(-15.07, -4.24) * mm]});
            skFitSpline(sketch, "E482", {"points": [v(-15.07, -4.24) * mm, v(-15, -4.24) * mm, v(-14.58, -4) * mm, v(-14.12, -3.7) * mm]});
            skLineSegment(sketch, "E483", {"start": v(-16.13, -0.42) * mm, "end": v(-17.44, -1.51) * mm});
            skLineSegment(sketch, "E484", {"start": v(-17.44, -1.51) * mm, "end": v(-16.92, -2.14) * mm});
            skLineSegment(sketch, "E485", {"start": v(-16.92, -2.14) * mm, "end": v(-16.13, -0.42) * mm});
            skFitSpline(sketch, "E486", {"points": [v(-19.91, -2.53) * mm, v(-19.22, -1.94) * mm, v(-18.67, -1.42) * mm, v(-18.68, -1.37) * mm]});
            skFitSpline(sketch, "E487", {"points": [v(-18.68, -1.37) * mm, v(-18.73, -1.25) * mm, v(-20.53, 0.9) * mm, v(-20.72, 1.06) * mm]});
            skFitSpline(sketch, "E488", {"points": [v(-20.72, 1.06) * mm, v(-20.83, 1.15) * mm, v(-21.17, 0.92) * mm, v(-22.14, 0.1) * mm]});
            skFitSpline(sketch, "E489", {"points": [v(-22.14, 0.1) * mm, v(-22.84, -0.5) * mm, v(-23.4, -1.03) * mm, v(-23.38, -1.08) * mm]});
            skFitSpline(sketch, "E490", {"points": [v(-23.38, -1.08) * mm, v(-23.32, -1.27) * mm, v(-21.37, -3.57) * mm, v(-21.27, -3.58) * mm]});
            skFitSpline(sketch, "E491", {"points": [v(-21.27, -3.58) * mm, v(-21.22, -3.58) * mm, v(-20.6, -3.1) * mm, v(-19.91, -2.53) * mm]});
            skFitSpline(sketch, "E492", {"points": [v(-25.75, 0.4) * mm, v(-26.36, 1.12) * mm, v(-26.88, 1.72) * mm, v(-26.89, 1.72) * mm]});
            skFitSpline(sketch, "E493", {"points": [v(-26.89, 1.72) * mm, v(-27.02, 1.72) * mm, v(-29.43, -0.43) * mm, v(-29.42, -0.54) * mm]});
            skFitSpline(sketch, "E494", {"points": [v(-29.42, -0.54) * mm, v(-29.4, -0.67) * mm, v(-27.39, -3.14) * mm, v(-27.3, -3.14) * mm]});
            skFitSpline(sketch, "E495", {"points": [v(-27.3, -3.14) * mm, v(-27.28, -3.14) * mm, v(-26.67, -2.64) * mm, v(-25.95, -2.03) * mm]});
            skLineSegment(sketch, "E496", {"start": v(-25.95, -2.03) * mm, "end": v(-24.63, -0.91) * mm});
            skLineSegment(sketch, "E497", {"start": v(-24.63, -0.91) * mm, "end": v(-25.75, 0.4) * mm});
            skLineSegment(sketch, "E498", {"start": v(-25.75, 0.4) * mm, "end": v(-25.95, -2.03) * mm});
            skFitSpline(sketch, "E499", {"points": [v(-29.7, -1.6) * mm, v(-29.96, -1.3) * mm, v(-30.18, -1.04) * mm, v(-30.2, -1.04) * mm]});
            skFitSpline(sketch, "E500", {"points": [v(-30.2, -1.04) * mm, v(-30.22, -1.04) * mm, v(-30.3, -1.11) * mm, v(-30.36, -1.2) * mm]});
            skFitSpline(sketch, "E501", {"points": [v(-30.36, -1.2) * mm, v(-30.47, -1.33) * mm, v(-30.39, -1.43) * mm, v(-29.9, -1.75) * mm]});
            skFitSpline(sketch, "E502", {"points": [v(-29.9, -1.75) * mm, v(-29.59, -1.97) * mm, v(-29.3, -2.15) * mm, v(-29.28, -2.15) * mm]});
            skFitSpline(sketch, "E503", {"points": [v(-29.28, -2.15) * mm, v(-29.26, -2.15) * mm, v(-29.45, -1.9) * mm, v(-29.7, -1.6) * mm]});
            skFitSpline(sketch, "E504", {"points": [v(-11.26, -0.36) * mm, v(-11.08, -0.01) * mm, v(-10.8, 0.7) * mm, v(-10.66, 1.22) * mm]});
            skFitSpline(sketch, "E505", {"points": [v(-10.66, 1.22) * mm, v(-10.35, 2.28) * mm, v(-10.33, 2.19) * mm, v(-11.06, 3.03) * mm]});
            skFitSpline(sketch, "E506", {"points": [v(-12.8, 2.37) * mm, v(-14.15, 1.25) * mm, v(-14.15, 1.25) * mm, v(-13.94, 1.01) * mm]});
            skFitSpline(sketch, "E507", {"points": [v(-13.94, 1.01) * mm, v(-13.82, 0.88) * mm, v(-13.31, 0.29) * mm, v(-12.8, -0.31) * mm]});
            skFitSpline(sketch, "E508", {"points": [v(-12.8, -0.31) * mm, v(-11.76, -1.54) * mm, v(-11.86, -1.54) * mm, v(-11.26, -0.36) * mm]});
            skLineSegment(sketch, "E509", {"start": v(-11.06, 3.03) * mm, "end": v(-11.46, 3.5) * mm});
            skLineSegment(sketch, "E510", {"start": v(-11.46, 3.5) * mm, "end": v(-12.8, 2.37) * mm});
            skLineSegment(sketch, "E511", {"start": v(-12.8, 2.37) * mm, "end": v(-11.06, 3.03) * mm});
            skFitSpline(sketch, "E512", {"points": [v(-30.81, -0.36) * mm, v(-30.81, -0.28) * mm, v(-32.37, 1.63) * mm, v(-32.84, 2.13) * mm]});
            skFitSpline(sketch, "E513", {"points": [v(-32.84, 2.13) * mm, v(-32.95, 2.24) * mm, v(-33.07, 2.2) * mm, v(-33.43, 1.88) * mm]});
            skFitSpline(sketch, "E514", {"points": [v(-33.26, 0.9) * mm, v(-32.91, 0.59) * mm, v(-32.32, 0.06) * mm, v(-31.93, -0.25) * mm]});
            skFitSpline(sketch, "E515", {"points": [v(-31.93, -0.25) * mm, v(-31.26, -0.8) * mm, v(-31.21, -0.82) * mm, v(-31.02, -0.64) * mm]});
            skFitSpline(sketch, "E516", {"points": [v(-31.02, -0.64) * mm, v(-30.9, -0.54) * mm, v(-30.81, -0.41) * mm, v(-30.81, -0.36) * mm]});
            skLineSegment(sketch, "E517", {"start": v(-33.43, 1.88) * mm, "end": v(-33.88, 1.5) * mm});
            skLineSegment(sketch, "E518", {"start": v(-33.88, 1.5) * mm, "end": v(-33.26, 0.9) * mm});
            skLineSegment(sketch, "E519", {"start": v(-33.26, 0.9) * mm, "end": v(-33.43, 1.88) * mm});
            skFitSpline(sketch, "E520", {"points": [v(-16.61, 0.24) * mm, v(-15.91, 0.83) * mm, v(-15.36, 1.35) * mm, v(-15.37, 1.4) * mm]});
            skFitSpline(sketch, "E521", {"points": [v(-15.37, 1.4) * mm, v(-15.42, 1.53) * mm, v(-17.07, 3.52) * mm, v(-17.33, 3.75) * mm]});
            skFitSpline(sketch, "E522", {"points": [v(-17.33, 3.75) * mm, v(-17.55, 3.95) * mm, v(-17.58, 3.93) * mm, v(-18.83, 2.88) * mm]});
            skFitSpline(sketch, "E523", {"points": [v(-18.83, 2.88) * mm, v(-19.53, 2.28) * mm, v(-20.1, 1.75) * mm, v(-20.07, 1.69) * mm]});
            skFitSpline(sketch, "E524", {"points": [v(-20.07, 1.69) * mm, v(-20, 1.5) * mm, v(-18.06, -0.8) * mm, v(-17.97, -0.82) * mm]});
            skFitSpline(sketch, "E525", {"points": [v(-17.97, -0.82) * mm, v(-17.92, -0.82) * mm, v(-17.3, -0.34) * mm, v(-16.61, 0.24) * mm]});
            skFitSpline(sketch, "E526", {"points": [v(-22.44, 3.17) * mm, v(-23.05, 3.89) * mm, v(-23.57, 4.48) * mm, v(-23.6, 4.48) * mm]});
            skFitSpline(sketch, "E527", {"points": [v(-23.6, 4.48) * mm, v(-23.62, 4.48) * mm, v(-24.21, 4) * mm, v(-24.9, 3.4) * mm]});
            skFitSpline(sketch, "E528", {"points": [v(-24.9, 3.4) * mm, v(-25.66, 2.77) * mm, v(-26.16, 2.27) * mm, v(-26.12, 2.19) * mm]});
            skFitSpline(sketch, "E529", {"points": [v(-26.12, 2.19) * mm, v(-26, 1.87) * mm, v(-24.02, -0.36) * mm, v(-23.91, -0.3) * mm]});
            skFitSpline(sketch, "E530", {"points": [v(-23.91, -0.3) * mm, v(-23.85, -0.26) * mm, v(-23.24, 0.24) * mm, v(-22.56, 0.81) * mm]});
            skLineSegment(sketch, "E531", {"start": v(-22.56, 0.81) * mm, "end": v(-21.32, 1.85) * mm});
            skLineSegment(sketch, "E532", {"start": v(-21.32, 1.85) * mm, "end": v(-22.44, 3.17) * mm});
            skLineSegment(sketch, "E533", {"start": v(-22.44, 3.17) * mm, "end": v(-22.56, 0.81) * mm});
            skFitSpline(sketch, "E534", {"points": [v(-28.76, 1.24) * mm, v(-28.07, 1.82) * mm, v(-27.5, 2.35) * mm, v(-27.5, 2.4) * mm]});
            skFitSpline(sketch, "E535", {"points": [v(-27.5, 2.4) * mm, v(-27.5, 2.48) * mm, v(-29.06, 4.4) * mm, v(-29.54, 4.9) * mm]});
            skFitSpline(sketch, "E536", {"points": [v(-29.54, 4.9) * mm, v(-29.65, 5.02) * mm, v(-29.9, 4.85) * mm, v(-30.93, 3.98) * mm]});
            skFitSpline(sketch, "E537", {"points": [v(-30.93, 3.98) * mm, v(-31.62, 3.4) * mm, v(-32.2, 2.87) * mm, v(-32.23, 2.82) * mm]});
            skFitSpline(sketch, "E538", {"points": [v(-32.23, 2.82) * mm, v(-32.26, 2.73) * mm, v(-30.17, 0.17) * mm, v(-30.07, 0.17) * mm]});
            skFitSpline(sketch, "E539", {"points": [v(-30.07, 0.17) * mm, v(-30.04, 0.17) * mm, v(-29.45, 0.65) * mm, v(-28.76, 1.24) * mm]});
            skFitSpline(sketch, "E540", {"points": [v(-13.25, 3.06) * mm, v(-12.58, 3.61) * mm, v(-12.04, 4.1) * mm, v(-12.04, 4.14) * mm]});
            skFitSpline(sketch, "E541", {"points": [v(-12.04, 4.14) * mm, v(-12.04, 4.24) * mm, v(-14.14, 6.69) * mm, v(-14.22, 6.69) * mm]});
            skFitSpline(sketch, "E542", {"points": [v(-14.22, 6.69) * mm, v(-14.38, 6.69) * mm, v(-16.8, 4.56) * mm, v(-16.76, 4.46) * mm]});
            skFitSpline(sketch, "E543", {"points": [v(-16.76, 4.46) * mm, v(-16.67, 4.17) * mm, v(-14.73, 1.96) * mm, v(-14.6, 2) * mm]});
            skFitSpline(sketch, "E544", {"points": [v(-14.6, 2) * mm, v(-14.53, 2.02) * mm, v(-13.92, 2.5) * mm, v(-13.25, 3.06) * mm]});
            skFitSpline(sketch, "E545", {"points": [v(-33.64, 2.97) * mm, v(-33.65, 3.06) * mm, v(-34.12, 3.68) * mm, v(-34.68, 4.35) * mm]});
            skFitSpline(sketch, "E546", {"points": [v(-34.68, 4.35) * mm, v(-35.81, 5.68) * mm, v(-35.69, 5.63) * mm, v(-36.43, 5) * mm]});
            skFitSpline(sketch, "E547", {"points": [v(-36.22, 4) * mm, v(-35.9, 3.63) * mm, v(-35.39, 3.04) * mm, v(-35.08, 2.7) * mm]});
            skLineSegment(sketch, "E548", {"start": v(-36.43, 5) * mm, "end": v(-36.8, 4.7) * mm});
            skLineSegment(sketch, "E549", {"start": v(-36.8, 4.7) * mm, "end": v(-36.22, 4) * mm});
            skLineSegment(sketch, "E550", {"start": v(-36.22, 4) * mm, "end": v(-36.43, 5) * mm});
            skFitSpline(sketch, "E551", {"points": [v(-34.07, 2.44) * mm, v(-33.83, 2.64) * mm, v(-33.63, 2.88) * mm, v(-33.64, 2.97) * mm]});
            skLineSegment(sketch, "E552", {"start": v(-35.08, 2.7) * mm, "end": v(-34.5, 2.08) * mm});
            skLineSegment(sketch, "E553", {"start": v(-34.5, 2.08) * mm, "end": v(-34.07, 2.44) * mm});
            skLineSegment(sketch, "E554", {"start": v(-34.07, 2.44) * mm, "end": v(-35.08, 2.7) * mm});
            skFitSpline(sketch, "E555", {"points": [v(-19.12, 5.93) * mm, v(-19.73, 6.65) * mm, v(-20.26, 7.24) * mm, v(-20.29, 7.24) * mm]});
            skFitSpline(sketch, "E556", {"points": [v(-20.29, 7.24) * mm, v(-20.32, 7.24) * mm, v(-20.91, 6.76) * mm, v(-21.6, 6.17) * mm]});
            skFitSpline(sketch, "E557", {"points": [v(-21.6, 6.17) * mm, v(-22.41, 5.5) * mm, v(-22.85, 5.05) * mm, v(-22.81, 4.95) * mm]});
            skFitSpline(sketch, "E558", {"points": [v(-22.81, 4.95) * mm, v(-22.78, 4.87) * mm, v(-22.3, 4.26) * mm, v(-21.74, 3.6) * mm]});
            skFitSpline(sketch, "E559", {"points": [v(-21.74, 3.6) * mm, v(-20.86, 2.56) * mm, v(-20.7, 2.41) * mm, v(-20.54, 2.52) * mm]});
            skFitSpline(sketch, "E560", {"points": [v(-20.54, 2.52) * mm, v(-20.44, 2.6) * mm, v(-19.83, 3.1) * mm, v(-19.18, 3.64) * mm]});
            skLineSegment(sketch, "E561", {"start": v(-19.18, 3.64) * mm, "end": v(-18.01, 4.62) * mm});
            skLineSegment(sketch, "E562", {"start": v(-18.01, 4.62) * mm, "end": v(-19.12, 5.93) * mm});
            skLineSegment(sketch, "E563", {"start": v(-19.12, 5.93) * mm, "end": v(-19.18, 3.64) * mm});
            skFitSpline(sketch, "E564", {"points": [v(-25.5, 3.99) * mm, v(-24.8, 4.57) * mm, v(-24.22, 5.09) * mm, v(-24.2, 5.15) * mm]});
            skFitSpline(sketch, "E565", {"points": [v(-24.2, 5.15) * mm, v(-24.17, 5.23) * mm, v(-25.42, 6.78) * mm, v(-26.18, 7.61) * mm]});
            skFitSpline(sketch, "E566", {"points": [v(-26.18, 7.61) * mm, v(-26.37, 7.81) * mm, v(-26.41, 7.79) * mm, v(-27.65, 6.74) * mm]});
            skFitSpline(sketch, "E567", {"points": [v(-27.65, 6.74) * mm, v(-28.36, 6.14) * mm, v(-28.93, 5.61) * mm, v(-28.93, 5.56) * mm]});
            skFitSpline(sketch, "E568", {"points": [v(-28.93, 5.56) * mm, v(-28.93, 5.47) * mm, v(-26.84, 2.93) * mm, v(-26.77, 2.93) * mm]});
            skFitSpline(sketch, "E569", {"points": [v(-26.77, 2.93) * mm, v(-26.75, 2.93) * mm, v(-26.18, 3.4) * mm, v(-25.5, 3.99) * mm]});
            skFitSpline(sketch, "E570", {"points": [v(-10.57, 3.7) * mm, v(-10.43, 3.52) * mm, v(-10.29, 3.38) * mm, v(-10.24, 3.38) * mm]});
            skFitSpline(sketch, "E571", {"points": [v(-10.24, 3.38) * mm, v(-10.2, 3.38) * mm, v(-10.16, 3.66) * mm, v(-10.16, 4) * mm]});
            skLineSegment(sketch, "E572", {"start": v(-10.16, 4) * mm, "end": v(-10.16, 4.63) * mm});
            skLineSegment(sketch, "E573", {"start": v(-10.16, 4.63) * mm, "end": v(-10.49, 4.32) * mm});
            skLineSegment(sketch, "E574", {"start": v(-10.49, 4.32) * mm, "end": v(-10.81, 4) * mm});
            skLineSegment(sketch, "E575", {"start": v(-10.81, 4) * mm, "end": v(-10.57, 3.7) * mm});
            skLineSegment(sketch, "E576", {"start": v(-10.57, 3.7) * mm, "end": v(-10.16, 4) * mm});
            skFitSpline(sketch, "E577", {"points": [v(-31.52, 4.55) * mm, v(-30.83, 5.14) * mm, v(-30.26, 5.66) * mm, v(-30.26, 5.7) * mm]});
            skFitSpline(sketch, "E578", {"points": [v(-30.26, 5.7) * mm, v(-30.26, 5.85) * mm, v(-32.38, 8.29) * mm, v(-32.48, 8.26) * mm]});
            skFitSpline(sketch, "E579", {"points": [v(-32.48, 8.26) * mm, v(-32.54, 8.24) * mm, v(-33.16, 7.75) * mm, v(-33.85, 7.17) * mm]});
            skFitSpline(sketch, "E580", {"points": [v(-34, 4.8) * mm, v(-33.38, 4.07) * mm, v(-32.86, 3.48) * mm, v(-32.84, 3.48) * mm]});
            skFitSpline(sketch, "E581", {"points": [v(-32.84, 3.48) * mm, v(-32.8, 3.48) * mm, v(-32.22, 3.97) * mm, v(-31.52, 4.55) * mm]});
            skLineSegment(sketch, "E582", {"start": v(-33.85, 7.17) * mm, "end": v(-35.1, 6.1) * mm});
            skLineSegment(sketch, "E583", {"start": v(-35.1, 6.1) * mm, "end": v(-34, 4.8) * mm});
            skLineSegment(sketch, "E584", {"start": v(-34, 4.8) * mm, "end": v(-33.85, 7.17) * mm});
            skFitSpline(sketch, "E585", {"points": [v(-10.2, 6.41) * mm, v(-10.3, 7.4) * mm, v(-10.6, 9) * mm, v(-10.76, 9.3) * mm]});
            skFitSpline(sketch, "E586", {"points": [v(-10.76, 9.3) * mm, v(-10.87, 9.54) * mm, v(-10.93, 9.51) * mm, v(-12.2, 8.43) * mm]});
            skFitSpline(sketch, "E587", {"points": [v(-12.2, 8.43) * mm, v(-12.93, 7.82) * mm, v(-13.51, 7.29) * mm, v(-13.5, 7.25) * mm]});
            skFitSpline(sketch, "E588", {"points": [v(-13.5, 7.25) * mm, v(-13.42, 7.06) * mm, v(-11.42, 4.72) * mm, v(-11.35, 4.73) * mm]});
            skFitSpline(sketch, "E589", {"points": [v(-11.35, 4.73) * mm, v(-11.3, 4.74) * mm, v(-11.01, 4.95) * mm, v(-10.7, 5.2) * mm]});
            skLineSegment(sketch, "E590", {"start": v(-10.7, 5.2) * mm, "end": v(-10.14, 5.64) * mm});
            skLineSegment(sketch, "E591", {"start": v(-10.14, 5.64) * mm, "end": v(-10.2, 6.41) * mm});
            skLineSegment(sketch, "E592", {"start": v(-10.2, 6.41) * mm, "end": v(-10.7, 5.2) * mm});
            skFitSpline(sketch, "E593", {"points": [v(-15.85, 6.43) * mm, v(-15.28, 6.9) * mm, v(-14.8, 7.34) * mm, v(-14.8, 7.4) * mm]});
            skFitSpline(sketch, "E594", {"points": [v(-14.8, 7.4) * mm, v(-14.8, 7.5) * mm, v(-16.88, 10) * mm, v(-16.99, 10) * mm]});
            skFitSpline(sketch, "E595", {"points": [v(-16.99, 10) * mm, v(-17.03, 10) * mm, v(-17.64, 9.5) * mm, v(-18.35, 8.9) * mm]});
            skFitSpline(sketch, "E596", {"points": [v(-17.15, 5.36) * mm, v(-17, 5.47) * mm, v(-16.42, 5.95) * mm, v(-15.85, 6.43) * mm]});
            skLineSegment(sketch, "E597", {"start": v(-18.35, 8.9) * mm, "end": v(-19.64, 7.82) * mm});
            skLineSegment(sketch, "E598", {"start": v(-19.64, 7.82) * mm, "end": v(-18.52, 6.49) * mm});
            skLineSegment(sketch, "E599", {"start": v(-18.52, 6.49) * mm, "end": v(-17.4, 5.16) * mm});
            skLineSegment(sketch, "E600", {"start": v(-17.4, 5.16) * mm, "end": v(-17.15, 5.36) * mm});
            skLineSegment(sketch, "E601", {"start": v(-17.15, 5.36) * mm, "end": v(-18.35, 8.9) * mm});
            skFitSpline(sketch, "E602", {"points": [v(-36.37, 6.2) * mm, v(-36.33, 6.3) * mm, v(-38.36, 8.78) * mm, v(-38.5, 8.8) * mm]});
            skFitSpline(sketch, "E603", {"points": [v(-38.5, 8.8) * mm, v(-38.53, 8.8) * mm, v(-38.7, 8.7) * mm, v(-38.88, 8.58) * mm]});
            skFitSpline(sketch, "E604", {"points": [v(-38.7, 7.5) * mm, v(-38.42, 7.03) * mm, v(-37.99, 6.36) * mm, v(-37.74, 6) * mm]});
            skLineSegment(sketch, "E605", {"start": v(-38.88, 8.58) * mm, "end": v(-39.2, 8.34) * mm});
            skLineSegment(sketch, "E606", {"start": v(-39.2, 8.34) * mm, "end": v(-38.7, 7.5) * mm});
            skLineSegment(sketch, "E607", {"start": v(-38.7, 7.5) * mm, "end": v(-38.88, 8.58) * mm});
            skFitSpline(sketch, "E608", {"points": [v(-36.84, 5.73) * mm, v(-36.6, 5.93) * mm, v(-36.38, 6.14) * mm, v(-36.37, 6.2) * mm]});
            skLineSegment(sketch, "E609", {"start": v(-37.74, 6) * mm, "end": v(-37.29, 5.37) * mm});
            skLineSegment(sketch, "E610", {"start": v(-37.29, 5.37) * mm, "end": v(-36.84, 5.73) * mm});
            skLineSegment(sketch, "E611", {"start": v(-36.84, 5.73) * mm, "end": v(-37.74, 6) * mm});
            skFitSpline(sketch, "E612", {"points": [v(-22.03, 6.9) * mm, v(-21.42, 7.4) * mm, v(-20.91, 7.87) * mm, v(-20.9, 7.92) * mm]});
            skFitSpline(sketch, "E613", {"points": [v(-20.9, 7.92) * mm, v(-20.86, 8) * mm, v(-22.95, 10.55) * mm, v(-23.06, 10.55) * mm]});
            skFitSpline(sketch, "E614", {"points": [v(-23.06, 10.55) * mm, v(-23.17, 10.55) * mm, v(-25.62, 8.43) * mm, v(-25.62, 8.33) * mm]});
            skFitSpline(sketch, "E615", {"points": [v(-25.62, 8.33) * mm, v(-25.62, 8.27) * mm, v(-25.14, 7.65) * mm, v(-24.55, 6.96) * mm]});
            skFitSpline(sketch, "E616", {"points": [v(-24.55, 6.96) * mm, v(-23.64, 5.87) * mm, v(-23.46, 5.71) * mm, v(-23.31, 5.83) * mm]});
            skFitSpline(sketch, "E617", {"points": [v(-23.31, 5.83) * mm, v(-23.21, 5.9) * mm, v(-22.64, 6.38) * mm, v(-22.03, 6.9) * mm]});
            skFitSpline(sketch, "E618", {"points": [v(-28.25, 7.3) * mm, v(-27.56, 7.88) * mm, v(-26.99, 8.4) * mm, v(-26.97, 8.44) * mm]});
            skFitSpline(sketch, "E619", {"points": [v(-26.97, 8.44) * mm, v(-26.95, 8.5) * mm, v(-28.5, 10.44) * mm, v(-29.05, 11.04) * mm]});
            skFitSpline(sketch, "E620", {"points": [v(-29.05, 11.04) * mm, v(-29.1, 11.09) * mm, v(-29.74, 10.62) * mm, v(-30.47, 10) * mm]});
            skFitSpline(sketch, "E621", {"points": [v(-30.69, 7.56) * mm, v(-30.07, 6.84) * mm, v(-29.56, 6.24) * mm, v(-29.54, 6.24) * mm]});
            skFitSpline(sketch, "E622", {"points": [v(-29.54, 6.24) * mm, v(-29.52, 6.24) * mm, v(-28.94, 6.72) * mm, v(-28.25, 7.3) * mm]});
            skLineSegment(sketch, "E623", {"start": v(-30.47, 10) * mm, "end": v(-31.8, 8.87) * mm});
            skLineSegment(sketch, "E624", {"start": v(-31.8, 8.87) * mm, "end": v(-30.69, 7.56) * mm});
            skLineSegment(sketch, "E625", {"start": v(-30.69, 7.56) * mm, "end": v(-30.47, 10) * mm});
            skFitSpline(sketch, "E626", {"points": [v(-34.28, 7.87) * mm, v(-33.59, 8.46) * mm, v(-33.02, 8.96) * mm, v(-33.02, 9) * mm]});
            skFitSpline(sketch, "E627", {"points": [v(-33.02, 9) * mm, v(-33.03, 9.14) * mm, v(-35.16, 11.6) * mm, v(-35.25, 11.57) * mm]});
            skFitSpline(sketch, "E628", {"points": [v(-35.25, 11.57) * mm, v(-35.3, 11.55) * mm, v(-35.92, 11.06) * mm, v(-36.62, 10.47) * mm]});
            skFitSpline(sketch, "E629", {"points": [v(-36.62, 10.47) * mm, v(-37.86, 9.42) * mm, v(-37.88, 9.4) * mm, v(-37.68, 9.18) * mm]});
            skFitSpline(sketch, "E630", {"points": [v(-37.68, 9.18) * mm, v(-37.57, 9.05) * mm, v(-37.07, 8.47) * mm, v(-36.56, 7.87) * mm]});
            skFitSpline(sketch, "E631", {"points": [v(-36.56, 7.87) * mm, v(-36.06, 7.28) * mm, v(-35.63, 6.8) * mm, v(-35.6, 6.8) * mm]});
            skFitSpline(sketch, "E632", {"points": [v(-35.6, 6.8) * mm, v(-35.57, 6.8) * mm, v(-34.98, 7.28) * mm, v(-34.28, 7.87) * mm]});
            skFitSpline(sketch, "E633", {"points": [v(-12.52, 11.47) * mm, v(-13.11, 12.18) * mm, v(-13.64, 12.76) * mm, v(-13.68, 12.76) * mm]});
            skFitSpline(sketch, "E634", {"points": [v(-13.68, 12.76) * mm, v(-13.8, 12.76) * mm, v(-16.3, 10.65) * mm, v(-16.27, 10.57) * mm]});
            skFitSpline(sketch, "E635", {"points": [v(-16.27, 10.57) * mm, v(-16.26, 10.53) * mm, v(-15.76, 9.92) * mm, v(-15.17, 9.2) * mm]});
            skLineSegment(sketch, "E636", {"start": v(-11.98, 9.7) * mm, "end": v(-11.43, 10.19) * mm});
            skLineSegment(sketch, "E637", {"start": v(-11.43, 10.19) * mm, "end": v(-12.52, 11.47) * mm});
            skLineSegment(sketch, "E638", {"start": v(-12.52, 11.47) * mm, "end": v(-11.98, 9.7) * mm});
            skFitSpline(sketch, "E639", {"points": [v(-13.32, 8.57) * mm, v(-12.89, 8.92) * mm, v(-12.29, 9.43) * mm, v(-11.98, 9.7) * mm]});
            skLineSegment(sketch, "E640", {"start": v(-15.17, 9.2) * mm, "end": v(-14.1, 7.92) * mm});
            skLineSegment(sketch, "E641", {"start": v(-14.1, 7.92) * mm, "end": v(-13.32, 8.57) * mm});
            skLineSegment(sketch, "E642", {"start": v(-13.32, 8.57) * mm, "end": v(-15.17, 9.2) * mm});
            skFitSpline(sketch, "E643", {"points": [v(-18.5, 9.83) * mm, v(-18, 10.26) * mm, v(-17.57, 10.65) * mm, v(-17.56, 10.7) * mm]});
            skFitSpline(sketch, "E644", {"points": [v(-17.56, 10.7) * mm, v(-17.56, 10.8) * mm, v(-19.66, 13.31) * mm, v(-19.75, 13.31) * mm]});
            skFitSpline(sketch, "E645", {"points": [v(-19.75, 13.31) * mm, v(-19.8, 13.31) * mm, v(-20.43, 12.8) * mm, v(-21.61, 11.8) * mm]});
            skFitSpline(sketch, "E646", {"points": [v(-19.81, 8.76) * mm, v(-19.61, 8.93) * mm, v(-19.02, 9.4) * mm, v(-18.5, 9.83) * mm]});
            skLineSegment(sketch, "E647", {"start": v(-21.61, 11.8) * mm, "end": v(-22.42, 11.12) * mm});
            skLineSegment(sketch, "E648", {"start": v(-22.42, 11.12) * mm, "end": v(-21.3, 9.8) * mm});
            skLineSegment(sketch, "E649", {"start": v(-21.3, 9.8) * mm, "end": v(-20.18, 8.46) * mm});
            skLineSegment(sketch, "E650", {"start": v(-20.18, 8.46) * mm, "end": v(-19.81, 8.76) * mm});
            skLineSegment(sketch, "E651", {"start": v(-19.81, 8.76) * mm, "end": v(-21.61, 11.8) * mm});
            skFitSpline(sketch, "E652", {"points": [v(-24.8, 10.2) * mm, v(-24.19, 10.72) * mm, v(-23.67, 11.17) * mm, v(-23.65, 11.22) * mm]});
            skFitSpline(sketch, "E653", {"points": [v(-23.65, 11.22) * mm, v(-23.61, 11.32) * mm, v(-25.7, 13.8) * mm, v(-25.84, 13.8) * mm]});
            skFitSpline(sketch, "E654", {"points": [v(-25.84, 13.8) * mm, v(-25.9, 13.8) * mm, v(-26.51, 13.32) * mm, v(-27.22, 12.73) * mm]});
            skFitSpline(sketch, "E655", {"points": [v(-27.38, 10.32) * mm, v(-26.4, 9.18) * mm, v(-26.23, 9.02) * mm, v(-26.08, 9.14) * mm]});
            skFitSpline(sketch, "E656", {"points": [v(-26.08, 9.14) * mm, v(-25.98, 9.22) * mm, v(-25.4, 9.7) * mm, v(-24.8, 10.2) * mm]});
            skLineSegment(sketch, "E657", {"start": v(-27.22, 12.73) * mm, "end": v(-28.5, 11.64) * mm});
            skLineSegment(sketch, "E658", {"start": v(-28.5, 11.64) * mm, "end": v(-27.38, 10.32) * mm});
            skLineSegment(sketch, "E659", {"start": v(-27.38, 10.32) * mm, "end": v(-27.22, 12.73) * mm});
            skFitSpline(sketch, "E660", {"points": [v(-39.26, 9.33) * mm, v(-39.08, 9.54) * mm, v(-39.08, 9.56) * mm, v(-39.27, 9.8) * mm]});
            skFitSpline(sketch, "E661", {"points": [v(-39.27, 9.8) * mm, v(-39.84, 10.52) * mm, v(-40.46, 11.21) * mm, v(-40.5, 11.17) * mm]});
            skFitSpline(sketch, "E662", {"points": [v(-40.5, 11.17) * mm, v(-40.56, 11.11) * mm, v(-39.63, 9.12) * mm, v(-39.54, 9.12) * mm]});
            skFitSpline(sketch, "E663", {"points": [v(-39.54, 9.12) * mm, v(-39.5, 9.12) * mm, v(-39.37, 9.21) * mm, v(-39.26, 9.33) * mm]});
            skFitSpline(sketch, "E664", {"points": [v(-31.01, 10.61) * mm, v(-30.32, 11.2) * mm, v(-29.75, 11.7) * mm, v(-29.73, 11.75) * mm]});
            skFitSpline(sketch, "E665", {"points": [v(-29.73, 11.75) * mm, v(-29.71, 11.8) * mm, v(-31.2, 13.65) * mm, v(-31.87, 14.4) * mm]});
            skFitSpline(sketch, "E666", {"points": [v(-31.87, 14.4) * mm, v(-31.88, 14.42) * mm, v(-32.5, 13.93) * mm, v(-33.24, 13.3) * mm]});
            skFitSpline(sketch, "E667", {"points": [v(-33.24, 13.3) * mm, v(-34.56, 12.18) * mm, v(-34.57, 12.17) * mm, v(-34.37, 11.94) * mm]});
            skFitSpline(sketch, "E668", {"points": [v(-34.37, 11.94) * mm, v(-34.26, 11.82) * mm, v(-33.75, 11.23) * mm, v(-33.25, 10.63) * mm]});
            skFitSpline(sketch, "E669", {"points": [v(-33.25, 10.63) * mm, v(-32.75, 10.04) * mm, v(-32.32, 9.56) * mm, v(-32.3, 9.56) * mm]});
            skFitSpline(sketch, "E670", {"points": [v(-32.3, 9.56) * mm, v(-32.28, 9.56) * mm, v(-31.7, 10.03) * mm, v(-31.01, 10.61) * mm]});
            skLineSegment(sketch, "E671", {"start": v(-39.26, 9.33) * mm, "end": v(-39.26, 9.33) * mm});
            skFitSpline(sketch, "E672", {"points": [v(-37.04, 11.18) * mm, v(-36.35, 11.77) * mm, v(-35.78, 12.28) * mm, v(-35.78, 12.31) * mm]});
            skFitSpline(sketch, "E673", {"points": [v(-35.78, 12.31) * mm, v(-35.78, 12.35) * mm, v(-36.28, 12.96) * mm, v(-36.88, 13.67) * mm]});
            skFitSpline(sketch, "E674", {"points": [v(-40.39, 12.42) * mm, v(-39.56, 11.38) * mm, v(-38.47, 10.12) * mm, v(-38.4, 10.12) * mm]});
            skFitSpline(sketch, "E675", {"points": [v(-38.4, 10.12) * mm, v(-38.35, 10.11) * mm, v(-37.74, 10.6) * mm, v(-37.04, 11.18) * mm]});
            skLineSegment(sketch, "E676", {"start": v(-36.88, 13.67) * mm, "end": v(-37.97, 14.97) * mm});
            skLineSegment(sketch, "E677", {"start": v(-37.97, 14.97) * mm, "end": v(-39.3, 13.85) * mm});
            skLineSegment(sketch, "E678", {"start": v(-39.3, 13.85) * mm, "end": v(-40.63, 12.73) * mm});
            skLineSegment(sketch, "E679", {"start": v(-40.63, 12.73) * mm, "end": v(-40.39, 12.42) * mm});
            skLineSegment(sketch, "E680", {"start": v(-40.39, 12.42) * mm, "end": v(-36.88, 13.67) * mm});
            skFitSpline(sketch, "E681", {"points": [v(-15.32, 12.53) * mm, v(-14.73, 13.03) * mm, v(-14.25, 13.47) * mm, v(-14.25, 13.5) * mm]});
            skFitSpline(sketch, "E682", {"points": [v(-14.25, 13.5) * mm, v(-14.25, 13.58) * mm, v(-16.37, 16.07) * mm, v(-16.45, 16.07) * mm]});
            skFitSpline(sketch, "E683", {"points": [v(-16.45, 16.07) * mm, v(-16.59, 16.07) * mm, v(-19.05, 13.94) * mm, v(-19.02, 13.85) * mm]});
            skFitSpline(sketch, "E684", {"points": [v(-19.02, 13.85) * mm, v(-19, 13.8) * mm, v(-18.51, 13.19) * mm, v(-17.92, 12.49) * mm]});
            skFitSpline(sketch, "E685", {"points": [v(-17.92, 12.49) * mm, v(-16.87, 11.23) * mm, v(-16.85, 11.22) * mm, v(-16.63, 11.42) * mm]});
            skFitSpline(sketch, "E686", {"points": [v(-16.63, 11.42) * mm, v(-16.5, 11.53) * mm, v(-15.91, 12.03) * mm, v(-15.32, 12.53) * mm]});
            skFitSpline(sketch, "E687", {"points": [v(-11.82, 12.7) * mm, v(-12.08, 13.34) * mm, v(-12.32, 13.86) * mm, v(-12.36, 13.86) * mm]});
            skFitSpline(sketch, "E688", {"points": [v(-12.36, 13.86) * mm, v(-12.4, 13.86) * mm, v(-12.56, 13.75) * mm, v(-12.73, 13.62) * mm]});
            skFitSpline(sketch, "E689", {"points": [v(-12.23, 12.41) * mm, v(-11.8, 11.88) * mm, v(-11.41, 11.47) * mm, v(-11.4, 11.5) * mm]});
            skFitSpline(sketch, "E690", {"points": [v(-11.4, 11.5) * mm, v(-11.37, 11.51) * mm, v(-11.57, 12.05) * mm, v(-11.82, 12.7) * mm]});
            skLineSegment(sketch, "E691", {"start": v(-12.73, 13.62) * mm, "end": v(-13.04, 13.37) * mm});
            skLineSegment(sketch, "E692", {"start": v(-13.04, 13.37) * mm, "end": v(-12.23, 12.41) * mm});
            skLineSegment(sketch, "E693", {"start": v(-12.23, 12.41) * mm, "end": v(-12.73, 13.62) * mm});
            skFitSpline(sketch, "E694", {"points": [v(-21.27, 13.15) * mm, v(-20.75, 13.57) * mm, v(-20.33, 13.95) * mm, v(-20.32, 14) * mm]});
            skFitSpline(sketch, "E695", {"points": [v(-20.32, 14) * mm, v(-20.32, 14.08) * mm, v(-22.4, 16.56) * mm, v(-22.5, 16.6) * mm]});
            skFitSpline(sketch, "E696", {"points": [v(-22.5, 16.6) * mm, v(-22.55, 16.61) * mm, v(-23.03, 16.25) * mm, v(-23.58, 15.78) * mm]});
            skFitSpline(sketch, "E697", {"points": [v(-23.58, 15.78) * mm, v(-24.12, 15.32) * mm, v(-24.71, 14.83) * mm, v(-24.88, 14.68) * mm]});
            skFitSpline(sketch, "E698", {"points": [v(-22.57, 12.07) * mm, v(-22.37, 12.24) * mm, v(-21.78, 12.72) * mm, v(-21.27, 13.15) * mm]});
            skLineSegment(sketch, "E699", {"start": v(-24.88, 14.68) * mm, "end": v(-25.2, 14.42) * mm});
            skLineSegment(sketch, "E700", {"start": v(-25.2, 14.42) * mm, "end": v(-24.07, 13.1) * mm});
            skLineSegment(sketch, "E701", {"start": v(-24.07, 13.1) * mm, "end": v(-22.94, 11.77) * mm});
            skLineSegment(sketch, "E702", {"start": v(-22.94, 11.77) * mm, "end": v(-22.57, 12.07) * mm});
            skLineSegment(sketch, "E703", {"start": v(-22.57, 12.07) * mm, "end": v(-24.88, 14.68) * mm});
            skFitSpline(sketch, "E704", {"points": [v(-27.55, 13.52) * mm, v(-26.95, 14.03) * mm, v(-26.43, 14.48) * mm, v(-26.42, 14.52) * mm]});
            skFitSpline(sketch, "E705", {"points": [v(-26.42, 14.52) * mm, v(-26.38, 14.61) * mm, v(-28.5, 17.12) * mm, v(-28.6, 17.12) * mm]});
            skFitSpline(sketch, "E706", {"points": [v(-28.6, 17.12) * mm, v(-28.66, 17.12) * mm, v(-29.27, 16.63) * mm, v(-29.98, 16.03) * mm]});
            skFitSpline(sketch, "E707", {"points": [v(-31.06, 14.7) * mm, v(-30.95, 14.58) * mm, v(-30.44, 13.99) * mm, v(-29.93, 13.4) * mm]});
            skFitSpline(sketch, "E708", {"points": [v(-29.93, 13.4) * mm, v(-29.14, 12.45) * mm, v(-29, 12.33) * mm, v(-28.84, 12.45) * mm]});
            skFitSpline(sketch, "E709", {"points": [v(-28.84, 12.45) * mm, v(-28.74, 12.53) * mm, v(-28.16, 13.01) * mm, v(-27.55, 13.52) * mm]});
            skLineSegment(sketch, "E710", {"start": v(-29.98, 16.03) * mm, "end": v(-31.27, 14.95) * mm});
            skLineSegment(sketch, "E711", {"start": v(-31.27, 14.95) * mm, "end": v(-31.06, 14.7) * mm});
            skLineSegment(sketch, "E712", {"start": v(-31.06, 14.7) * mm, "end": v(-29.98, 16.03) * mm});
            skFitSpline(sketch, "E713", {"points": [v(-33.83, 13.88) * mm, v(-33.17, 14.43) * mm, v(-32.59, 14.92) * mm, v(-32.53, 14.98) * mm]});
            skFitSpline(sketch, "E714", {"points": [v(-32.53, 14.98) * mm, v(-32.48, 15.03) * mm, v(-32.9, 15.63) * mm, v(-33.52, 16.37) * mm]});
            skFitSpline(sketch, "E715", {"points": [v(-33.52, 16.37) * mm, v(-34.12, 17.09) * mm, v(-34.62, 17.7) * mm, v(-34.63, 17.71) * mm]});
            skFitSpline(sketch, "E716", {"points": [v(-34.63, 17.71) * mm, v(-34.65, 17.74) * mm, v(-35.26, 17.25) * mm, v(-36, 16.63) * mm]});
            skFitSpline(sketch, "E717", {"points": [v(-37.11, 15.23) * mm, v(-36.44, 14.37) * mm, v(-35.16, 12.88) * mm, v(-35.1, 12.88) * mm]});
            skFitSpline(sketch, "E718", {"points": [v(-35.1, 12.88) * mm, v(-35.06, 12.87) * mm, v(-34.48, 13.32) * mm, v(-33.83, 13.88) * mm]});
            skLineSegment(sketch, "E719", {"start": v(-36, 16.63) * mm, "end": v(-37.32, 15.5) * mm});
            skLineSegment(sketch, "E720", {"start": v(-37.32, 15.5) * mm, "end": v(-37.11, 15.23) * mm});
            skLineSegment(sketch, "E721", {"start": v(-37.11, 15.23) * mm, "end": v(-36, 16.63) * mm});
            skFitSpline(sketch, "E722", {"points": [v(-39.95, 14.37) * mm, v(-39.33, 14.9) * mm, v(-38.75, 15.4) * mm, v(-38.66, 15.47) * mm]});
            skFitSpline(sketch, "E723", {"points": [v(-38.66, 15.47) * mm, v(-38.53, 15.6) * mm, v(-38.67, 15.81) * mm, v(-39.59, 16.9) * mm]});
            skFitSpline(sketch, "E724", {"points": [v(-39.59, 16.9) * mm, v(-40.18, 17.6) * mm, v(-40.7, 18.2) * mm, v(-40.74, 18.22) * mm]});
            skFitSpline(sketch, "E725", {"points": [v(-40.74, 18.22) * mm, v(-40.79, 18.25) * mm, v(-41.07, 18.07) * mm, v(-41.37, 17.82) * mm]});
            skFitSpline(sketch, "E726", {"points": [v(-41.37, 17.82) * mm, v(-41.99, 17.3) * mm, v(-41.98, 17.33) * mm, v(-41.68, 15.3) * mm]});
            skFitSpline(sketch, "E727", {"points": [v(-41.68, 15.3) * mm, v(-41.5, 14.06) * mm, v(-41.33, 13.42) * mm, v(-41.18, 13.42) * mm]});
            skFitSpline(sketch, "E728", {"points": [v(-41.18, 13.42) * mm, v(-41.13, 13.42) * mm, v(-40.57, 13.85) * mm, v(-39.95, 14.37) * mm]});
            skFitSpline(sketch, "E729", {"points": [v(-13.11, 15.4) * mm, v(-13.34, 15.8) * mm, v(-13.75, 16.5) * mm, v(-14.03, 16.94) * mm]});
            skLineSegment(sketch, "E730", {"start": v(-13.09, 14.38) * mm, "end": v(-12.71, 14.68) * mm});
            skLineSegment(sketch, "E731", {"start": v(-12.71, 14.68) * mm, "end": v(-13.11, 15.4) * mm});
            skLineSegment(sketch, "E732", {"start": v(-13.11, 15.4) * mm, "end": v(-13.09, 14.38) * mm});
            skFitSpline(sketch, "E733", {"points": [v(-15.14, 17.23) * mm, v(-15.47, 16.95) * mm, v(-15.72, 16.67) * mm, v(-15.7, 16.62) * mm]});
            skFitSpline(sketch, "E734", {"points": [v(-15.7, 16.62) * mm, v(-15.66, 16.46) * mm, v(-13.64, 14.09) * mm, v(-13.55, 14.09) * mm]});
            skFitSpline(sketch, "E735", {"points": [v(-13.55, 14.09) * mm, v(-13.5, 14.09) * mm, v(-13.3, 14.22) * mm, v(-13.09, 14.38) * mm]});
            skLineSegment(sketch, "E736", {"start": v(-14.03, 16.94) * mm, "end": v(-14.54, 17.74) * mm});
            skLineSegment(sketch, "E737", {"start": v(-14.54, 17.74) * mm, "end": v(-15.14, 17.23) * mm});
            skLineSegment(sketch, "E738", {"start": v(-15.14, 17.23) * mm, "end": v(-14.03, 16.94) * mm});
            skFitSpline(sketch, "E739", {"points": [v(-18.08, 15.85) * mm, v(-17.43, 16.4) * mm, v(-17.04, 16.8) * mm, v(-17.08, 16.88) * mm]});
            skFitSpline(sketch, "E740", {"points": [v(-17.08, 16.88) * mm, v(-17.23, 17.13) * mm, v(-19.16, 19.39) * mm, v(-19.22, 19.39) * mm]});
            skFitSpline(sketch, "E741", {"points": [v(-19.22, 19.39) * mm, v(-19.27, 19.39) * mm, v(-21.58, 17.49) * mm, v(-21.85, 17.23) * mm]});
            skFitSpline(sketch, "E742", {"points": [v(-21.85, 17.23) * mm, v(-21.87, 17.2) * mm, v(-21.38, 16.6) * mm, v(-20.75, 15.86) * mm]});
            skFitSpline(sketch, "E743", {"points": [v(-20.75, 15.86) * mm, v(-19.63, 14.53) * mm, v(-19.62, 14.52) * mm, v(-19.4, 14.73) * mm]});
            skFitSpline(sketch, "E744", {"points": [v(-19.4, 14.73) * mm, v(-19.26, 14.84) * mm, v(-18.67, 15.34) * mm, v(-18.08, 15.85) * mm]});
            skFitSpline(sketch, "E745", {"points": [v(-24.03, 16.46) * mm, v(-23.51, 16.89) * mm, v(-23.09, 17.26) * mm, v(-23.09, 17.3) * mm]});
            skFitSpline(sketch, "E746", {"points": [v(-23.09, 17.3) * mm, v(-23.08, 17.4) * mm, v(-25.2, 19.88) * mm, v(-25.3, 19.88) * mm]});
            skFitSpline(sketch, "E747", {"points": [v(-25.3, 19.88) * mm, v(-25.44, 19.88) * mm, v(-27.93, 17.8) * mm, v(-27.9, 17.7) * mm]});
            skFitSpline(sketch, "E748", {"points": [v(-27.9, 17.7) * mm, v(-27.9, 17.67) * mm, v(-27.4, 17.06) * mm, v(-26.8, 16.35) * mm]});
            skFitSpline(sketch, "E749", {"points": [v(-25.34, 15.38) * mm, v(-25.14, 15.55) * mm, v(-24.55, 16.03) * mm, v(-24.03, 16.46) * mm]});
            skLineSegment(sketch, "E750", {"start": v(-26.8, 16.35) * mm, "end": v(-25.71, 15.07) * mm});
            skLineSegment(sketch, "E751", {"start": v(-25.71, 15.07) * mm, "end": v(-25.34, 15.38) * mm});
            skLineSegment(sketch, "E752", {"start": v(-25.34, 15.38) * mm, "end": v(-26.8, 16.35) * mm});
            skFitSpline(sketch, "E753", {"points": [v(-30.48, 16.7) * mm, v(-29.78, 17.28) * mm, v(-29.2, 17.8) * mm, v(-29.2, 17.85) * mm]});
            skFitSpline(sketch, "E754", {"points": [v(-29.2, 17.85) * mm, v(-29.2, 17.9) * mm, v(-29.66, 18.47) * mm, v(-30.2, 19.12) * mm]});
            skFitSpline(sketch, "E755", {"points": [v(-30.2, 19.12) * mm, v(-30.75, 19.77) * mm, v(-31.23, 20.35) * mm, v(-31.27, 20.41) * mm]});
            skFitSpline(sketch, "E756", {"points": [v(-31.27, 20.41) * mm, v(-31.33, 20.51) * mm, v(-33.53, 18.79) * mm, v(-33.88, 18.37) * mm]});
            skFitSpline(sketch, "E757", {"points": [v(-33.88, 18.37) * mm, v(-33.97, 18.25) * mm, v(-33.76, 17.94) * mm, v(-32.93, 16.93) * mm]});
            skFitSpline(sketch, "E758", {"points": [v(-32.93, 16.93) * mm, v(-32.34, 16.22) * mm, v(-31.83, 15.64) * mm, v(-31.8, 15.64) * mm]});
            skFitSpline(sketch, "E759", {"points": [v(-31.8, 15.64) * mm, v(-31.77, 15.63) * mm, v(-31.17, 16.11) * mm, v(-30.48, 16.7) * mm]});
            skFitSpline(sketch, "E760", {"points": [v(-36.6, 17.19) * mm, v(-35.93, 17.74) * mm, v(-35.35, 18.24) * mm, v(-35.3, 18.29) * mm]});
            skFitSpline(sketch, "E761", {"points": [v(-35.3, 18.29) * mm, v(-35.21, 18.36) * mm, v(-37.16, 20.82) * mm, v(-37.44, 20.99) * mm]});
            skFitSpline(sketch, "E762", {"points": [v(-37.44, 20.99) * mm, v(-37.56, 21.06) * mm, v(-40.1, 18.93) * mm, v(-40.06, 18.8) * mm]});
            skFitSpline(sketch, "E763", {"points": [v(-40.06, 18.8) * mm, v(-40, 18.64) * mm, v(-37.94, 16.19) * mm, v(-37.86, 16.19) * mm]});
            skFitSpline(sketch, "E764", {"points": [v(-37.86, 16.19) * mm, v(-37.82, 16.18) * mm, v(-37.25, 16.64) * mm, v(-36.6, 17.19) * mm]});
            skFitSpline(sketch, "E765", {"points": [v(-15.1, 18.55) * mm, v(-15.9, 19.59) * mm, v(-16.71, 20.6) * mm, v(-16.94, 20.81) * mm]});
            skFitSpline(sketch, "E766", {"points": [v(-16.94, 20.81) * mm, v(-17.26, 21.1) * mm, v(-17.3, 21.1) * mm, v(-18.15, 20.34) * mm]});
            skFitSpline(sketch, "E767", {"points": [v(-15.67, 17.86) * mm, v(-15.26, 18.22) * mm, v(-15.05, 18.47) * mm, v(-15.1, 18.55) * mm]});
            skLineSegment(sketch, "E768", {"start": v(-18.15, 20.34) * mm, "end": v(-18.58, 19.97) * mm});
            skLineSegment(sketch, "E769", {"start": v(-18.58, 19.97) * mm, "end": v(-17.45, 18.63) * mm});
            skLineSegment(sketch, "E770", {"start": v(-17.45, 18.63) * mm, "end": v(-16.32, 17.3) * mm});
            skLineSegment(sketch, "E771", {"start": v(-16.32, 17.3) * mm, "end": v(-15.67, 17.86) * mm});
            skLineSegment(sketch, "E772", {"start": v(-15.67, 17.86) * mm, "end": v(-18.15, 20.34) * mm});
            skFitSpline(sketch, "E773", {"points": [v(-19.9, 20.25) * mm, v(-20.3, 20.76) * mm, v(-21.9, 22.65) * mm, v(-21.97, 22.67) * mm]});
            skFitSpline(sketch, "E774", {"points": [v(-21.97, 22.67) * mm, v(-22.06, 22.71) * mm, v(-24.57, 20.6) * mm, v(-24.57, 20.5) * mm]});
            skFitSpline(sketch, "E775", {"points": [v(-24.57, 20.5) * mm, v(-24.57, 20.44) * mm, v(-24.08, 19.83) * mm, v(-23.49, 19.12) * mm]});
            skFitSpline(sketch, "E776", {"points": [v(-21.08, 18.95) * mm, v(-19.92, 19.93) * mm, v(-19.77, 20.1) * mm, v(-19.9, 20.25) * mm]});
            skLineSegment(sketch, "E777", {"start": v(-23.49, 19.12) * mm, "end": v(-22.4, 17.84) * mm});
            skLineSegment(sketch, "E778", {"start": v(-22.4, 17.84) * mm, "end": v(-21.08, 18.95) * mm});
            skLineSegment(sketch, "E779", {"start": v(-21.08, 18.95) * mm, "end": v(-23.49, 19.12) * mm});
            skFitSpline(sketch, "E780", {"points": [v(-27.12, 19.5) * mm, v(-26.43, 20.07) * mm, v(-25.86, 20.58) * mm, v(-25.88, 20.63) * mm]});
            skFitSpline(sketch, "E781", {"points": [v(-25.88, 20.63) * mm, v(-25.92, 20.79) * mm, v(-28, 23.24) * mm, v(-28.08, 23.22) * mm]});
            skFitSpline(sketch, "E782", {"points": [v(-28.08, 23.22) * mm, v(-28.24, 23.18) * mm, v(-30.69, 21.1) * mm, v(-30.67, 21.02) * mm]});
            skFitSpline(sketch, "E783", {"points": [v(-30.67, 21.02) * mm, v(-30.62, 20.85) * mm, v(-28.54, 18.4) * mm, v(-28.47, 18.43) * mm]});
            skFitSpline(sketch, "E784", {"points": [v(-28.47, 18.43) * mm, v(-28.42, 18.44) * mm, v(-27.82, 18.92) * mm, v(-27.12, 19.5) * mm]});
            skFitSpline(sketch, "E785", {"points": [v(-41.9, 19.16) * mm, v(-42.04, 18.43) * mm, v(-41.95, 18.33) * mm, v(-41.54, 18.76) * mm]});
            skLineSegment(sketch, "E786", {"start": v(-41.54, 18.76) * mm, "end": v(-41.3, 19.02) * mm});
            skLineSegment(sketch, "E787", {"start": v(-41.3, 19.02) * mm, "end": v(-41.56, 19.26) * mm});
            skLineSegment(sketch, "E788", {"start": v(-41.56, 19.26) * mm, "end": v(-41.82, 19.5) * mm});
            skLineSegment(sketch, "E789", {"start": v(-41.82, 19.5) * mm, "end": v(-41.9, 19.16) * mm});
            skLineSegment(sketch, "E790", {"start": v(-41.9, 19.16) * mm, "end": v(-41.54, 18.76) * mm});
            skFitSpline(sketch, "E791", {"points": [v(-33.24, 20) * mm, v(-32.54, 20.6) * mm, v(-31.95, 21.09) * mm, v(-31.93, 21.1) * mm]});
            skFitSpline(sketch, "E792", {"points": [v(-31.93, 21.1) * mm, v(-31.88, 21.15) * mm, v(-33.97, 23.65) * mm, v(-34.13, 23.75) * mm]});
            skFitSpline(sketch, "E793", {"points": [v(-34.13, 23.75) * mm, v(-34.26, 23.83) * mm, v(-36.8, 21.71) * mm, v(-36.75, 21.57) * mm]});
            skFitSpline(sketch, "E794", {"points": [v(-36.75, 21.57) * mm, v(-36.7, 21.42) * mm, v(-34.64, 18.95) * mm, v(-34.56, 18.95) * mm]});
            skFitSpline(sketch, "E795", {"points": [v(-34.56, 18.95) * mm, v(-34.53, 18.95) * mm, v(-33.93, 19.42) * mm, v(-33.24, 20) * mm]});
            skFitSpline(sketch, "E796", {"points": [v(-39.29, 20.64) * mm, v(-38.63, 21.19) * mm, v(-38.1, 21.67) * mm, v(-38.1, 21.73) * mm]});
            skFitSpline(sketch, "E797", {"points": [v(-38.1, 21.73) * mm, v(-38.1, 21.78) * mm, v(-38.58, 22.4) * mm, v(-39.17, 23.1) * mm]});
            skFitSpline(sketch, "E798", {"points": [v(-40.6, 23.74) * mm, v(-40.98, 23.06) * mm, v(-41.63, 21.22) * mm, v(-41.63, 20.82) * mm]});
            skFitSpline(sketch, "E799", {"points": [v(-41.63, 20.82) * mm, v(-41.63, 20.53) * mm, v(-40.75, 19.48) * mm, v(-40.59, 19.58) * mm]});
            skFitSpline(sketch, "E800", {"points": [v(-40.59, 19.58) * mm, v(-40.53, 19.62) * mm, v(-39.94, 20.1) * mm, v(-39.29, 20.64) * mm]});
            skLineSegment(sketch, "E801", {"start": v(-39.17, 23.1) * mm, "end": v(-40.23, 24.37) * mm});
            skLineSegment(sketch, "E802", {"start": v(-40.23, 24.37) * mm, "end": v(-40.6, 23.74) * mm});
            skLineSegment(sketch, "E803", {"start": v(-40.6, 23.74) * mm, "end": v(-39.17, 23.1) * mm});
            skFitSpline(sketch, "E804", {"points": [v(-18.13, 22.13) * mm, v(-18.33, 22.33) * mm, v(-18.91, 22.87) * mm, v(-19.42, 23.32) * mm]});
            skFitSpline(sketch, "E805", {"points": [v(-20.83, 23.72) * mm, v(-21.1, 23.5) * mm, v(-21.3, 23.28) * mm, v(-21.29, 23.24) * mm]});
            skFitSpline(sketch, "E806", {"points": [v(-21.29, 23.24) * mm, v(-21.27, 23.2) * mm, v(-20.77, 22.58) * mm, v(-20.17, 21.88) * mm]});
            skLineSegment(sketch, "E807", {"start": v(-19.42, 23.32) * mm, "end": v(-20.34, 24.13) * mm});
            skLineSegment(sketch, "E808", {"start": v(-20.34, 24.13) * mm, "end": v(-20.83, 23.72) * mm});
            skLineSegment(sketch, "E809", {"start": v(-20.83, 23.72) * mm, "end": v(-19.42, 23.32) * mm});
            skLineSegment(sketch, "E810", {"start": v(-20.17, 21.88) * mm, "end": v(-19.09, 20.6) * mm});
            skLineSegment(sketch, "E811", {"start": v(-19.09, 20.6) * mm, "end": v(-18.43, 21.17) * mm});
            skLineSegment(sketch, "E812", {"start": v(-18.43, 21.17) * mm, "end": v(-17.77, 21.74) * mm});
            skLineSegment(sketch, "E813", {"start": v(-17.77, 21.74) * mm, "end": v(-18.13, 22.13) * mm});
            skLineSegment(sketch, "E814", {"start": v(-18.13, 22.13) * mm, "end": v(-20.17, 21.88) * mm});
            skFitSpline(sketch, "E815", {"points": [v(-22.77, 23.7) * mm, v(-23.46, 24.55) * mm, v(-24.69, 26) * mm, v(-24.74, 26) * mm]});
            skFitSpline(sketch, "E816", {"points": [v(-24.74, 26) * mm, v(-24.85, 26.02) * mm, v(-27.33, 23.91) * mm, v(-27.33, 23.8) * mm]});
            skFitSpline(sketch, "E817", {"points": [v(-27.33, 23.8) * mm, v(-27.33, 23.72) * mm, v(-25.29, 21.18) * mm, v(-25.2, 21.16) * mm]});
            skFitSpline(sketch, "E818", {"points": [v(-25.2, 21.16) * mm, v(-25.18, 21.16) * mm, v(-24.57, 21.65) * mm, v(-23.84, 22.27) * mm]});
            skLineSegment(sketch, "E819", {"start": v(-23.84, 22.27) * mm, "end": v(-22.52, 23.38) * mm});
            skLineSegment(sketch, "E820", {"start": v(-22.52, 23.38) * mm, "end": v(-22.77, 23.7) * mm});
            skLineSegment(sketch, "E821", {"start": v(-22.77, 23.7) * mm, "end": v(-23.84, 22.27) * mm});
            skFitSpline(sketch, "E822", {"points": [v(-29.94, 22.77) * mm, v(-29.23, 23.36) * mm, v(-28.64, 23.86) * mm, v(-28.62, 23.87) * mm]});
            skFitSpline(sketch, "E823", {"points": [v(-28.62, 23.87) * mm, v(-28.57, 23.9) * mm, v(-30.67, 26.42) * mm, v(-30.83, 26.52) * mm]});
            skFitSpline(sketch, "E824", {"points": [v(-30.83, 26.52) * mm, v(-30.96, 26.6) * mm, v(-33.48, 24.48) * mm, v(-33.43, 24.33) * mm]});
            skFitSpline(sketch, "E825", {"points": [v(-33.43, 24.33) * mm, v(-33.4, 24.2) * mm, v(-31.33, 21.71) * mm, v(-31.27, 21.7) * mm]});
            skFitSpline(sketch, "E826", {"points": [v(-31.27, 21.7) * mm, v(-31.24, 21.7) * mm, v(-30.65, 22.19) * mm, v(-29.94, 22.77) * mm]});
            skFitSpline(sketch, "E827", {"points": [v(-36.02, 23.38) * mm, v(-35.37, 23.93) * mm, v(-34.82, 24.42) * mm, v(-34.8, 24.48) * mm]});
            skFitSpline(sketch, "E828", {"points": [v(-34.8, 24.48) * mm, v(-34.78, 24.54) * mm, v(-35.28, 25.2) * mm, v(-35.9, 25.93) * mm]});
            skFitSpline(sketch, "E829", {"points": [v(-35.9, 25.93) * mm, v(-36.52, 26.68) * mm, v(-37.05, 27.3) * mm, v(-37.06, 27.32) * mm]});
            skFitSpline(sketch, "E830", {"points": [v(-37.06, 27.32) * mm, v(-37.17, 27.47) * mm, v(-38.76, 26.22) * mm, v(-39.33, 25.54) * mm]});
            skFitSpline(sketch, "E831", {"points": [v(-38.57, 23.66) * mm, v(-37.93, 22.9) * mm, v(-37.36, 22.3) * mm, v(-37.3, 22.32) * mm]});
            skFitSpline(sketch, "E832", {"points": [v(-37.3, 22.32) * mm, v(-37.25, 22.36) * mm, v(-36.68, 22.83) * mm, v(-36.02, 23.38) * mm]});
            skLineSegment(sketch, "E833", {"start": v(-39.33, 25.54) * mm, "end": v(-39.73, 25.06) * mm});
            skLineSegment(sketch, "E834", {"start": v(-39.73, 25.06) * mm, "end": v(-38.57, 23.66) * mm});
            skLineSegment(sketch, "E835", {"start": v(-38.57, 23.66) * mm, "end": v(-39.33, 25.54) * mm});
            skFitSpline(sketch, "E836", {"points": [v(-21.55, 25.02) * mm, v(-22.2, 25.5) * mm, v(-23.98, 26.59) * mm, v(-24.02, 26.54) * mm]});
            skFitSpline(sketch, "E837", {"points": [v(-24.02, 26.54) * mm, v(-24.04, 26.52) * mm, v(-23.58, 25.93) * mm, v(-22.99, 25.23) * mm]});
            skFitSpline(sketch, "E838", {"points": [v(-22.99, 25.23) * mm, v(-21.85, 23.86) * mm, v(-21.83, 23.85) * mm, v(-21.33, 24.4) * mm]});
            skLineSegment(sketch, "E839", {"start": v(-21.33, 24.4) * mm, "end": v(-21.07, 24.67) * mm});
            skLineSegment(sketch, "E840", {"start": v(-21.07, 24.67) * mm, "end": v(-21.55, 25.02) * mm});
            skLineSegment(sketch, "E841", {"start": v(-21.55, 25.02) * mm, "end": v(-21.33, 24.4) * mm});
            skFitSpline(sketch, "E842", {"points": [v(-25.63, 27.12) * mm, v(-25.93, 27.5) * mm, v(-26.13, 27.6) * mm, v(-27.19, 27.94) * mm]});
            skFitSpline(sketch, "E843", {"points": [v(-27.19, 27.94) * mm, v(-27.85, 28.15) * mm, v(-28.5, 28.33) * mm, v(-28.62, 28.33) * mm]});
            skFitSpline(sketch, "E844", {"points": [v(-28.62, 28.33) * mm, v(-28.8, 28.33) * mm, v(-29.97, 27.48) * mm, v(-30.15, 27.2) * mm]});
            skFitSpline(sketch, "E845", {"points": [v(-30.15, 27.2) * mm, v(-30.2, 27.14) * mm, v(-28.06, 24.48) * mm, v(-27.96, 24.47) * mm]});
            skFitSpline(sketch, "E846", {"points": [v(-27.96, 24.47) * mm, v(-27.94, 24.47) * mm, v(-27.33, 24.97) * mm, v(-26.6, 25.58) * mm]});
            skLineSegment(sketch, "E847", {"start": v(-26.6, 25.58) * mm, "end": v(-25.29, 26.69) * mm});
            skLineSegment(sketch, "E848", {"start": v(-25.29, 26.69) * mm, "end": v(-25.63, 27.12) * mm});
            skLineSegment(sketch, "E849", {"start": v(-25.63, 27.12) * mm, "end": v(-26.6, 25.58) * mm});
            skFitSpline(sketch, "E850", {"points": [v(-32.63, 26.23) * mm, v(-32.03, 26.73) * mm, v(-31.51, 27.19) * mm, v(-31.5, 27.24) * mm]});
            skFitSpline(sketch, "E851", {"points": [v(-31.5, 27.24) * mm, v(-31.47, 27.3) * mm, v(-31.7, 27.63) * mm, v(-31.99, 28) * mm]});
            skFitSpline(sketch, "E852", {"points": [v(-31.99, 28) * mm, v(-32.49, 28.6) * mm, v(-32.55, 28.65) * mm, v(-33, 28.66) * mm]});
            skFitSpline(sketch, "E853", {"points": [v(-33, 28.66) * mm, v(-33.26, 28.66) * mm, v(-33.7, 28.6) * mm, v(-34, 28.54) * mm]});
            skFitSpline(sketch, "E854", {"points": [v(-34, 28.54) * mm, v(-34.77, 28.36) * mm, v(-36.21, 27.88) * mm, v(-36.27, 27.79) * mm]});
            skFitSpline(sketch, "E855", {"points": [v(-36.27, 27.79) * mm, v(-36.3, 27.74) * mm, v(-35.82, 27.1) * mm, v(-35.2, 26.37) * mm]});
            skFitSpline(sketch, "E856", {"points": [v(-35.2, 26.37) * mm, v(-34.23, 25.21) * mm, v(-34.05, 25.05) * mm, v(-33.9, 25.17) * mm]});
            skFitSpline(sketch, "E857", {"points": [v(-33.9, 25.17) * mm, v(-33.81, 25.25) * mm, v(-33.24, 25.73) * mm, v(-32.63, 26.23) * mm]});
            skFitSpline(sketch, "E858", {"points": [v(-29.93, 28.56) * mm, v(-29.93, 28.63) * mm, v(-31.38, 28.79) * mm, v(-31.46, 28.72) * mm]});
            skFitSpline(sketch, "E859", {"points": [v(-31.46, 28.72) * mm, v(-31.48, 28.7) * mm, v(-31.33, 28.48) * mm, v(-31.14, 28.23) * mm]});
            skFitSpline(sketch, "E860", {"points": [v(-30.35, 28.14) * mm, v(-30.12, 28.32) * mm, v(-29.93, 28.51) * mm, v(-29.93, 28.56) * mm]});
            skLineSegment(sketch, "E861", {"start": v(-31.14, 28.23) * mm, "end": v(-30.78, 27.8) * mm});
            skLineSegment(sketch, "E862", {"start": v(-30.78, 27.8) * mm, "end": v(-30.35, 28.14) * mm});
            skLineSegment(sketch, "E863", {"start": v(-30.35, 28.14) * mm, "end": v(-31.14, 28.23) * mm});
            skSolve(sketch);
        }
        {
            var Q0;
            Q0 = qSketchRegion(id + "F2", true);
            extrude(context, id + "F3", {"entities" : qUnion([Q0]), "operationType" : NewBodyOperationType.ADD, "depth" : 2.3 * mm, "offsetDistance" : 25.4 * mm});
        }
    });
